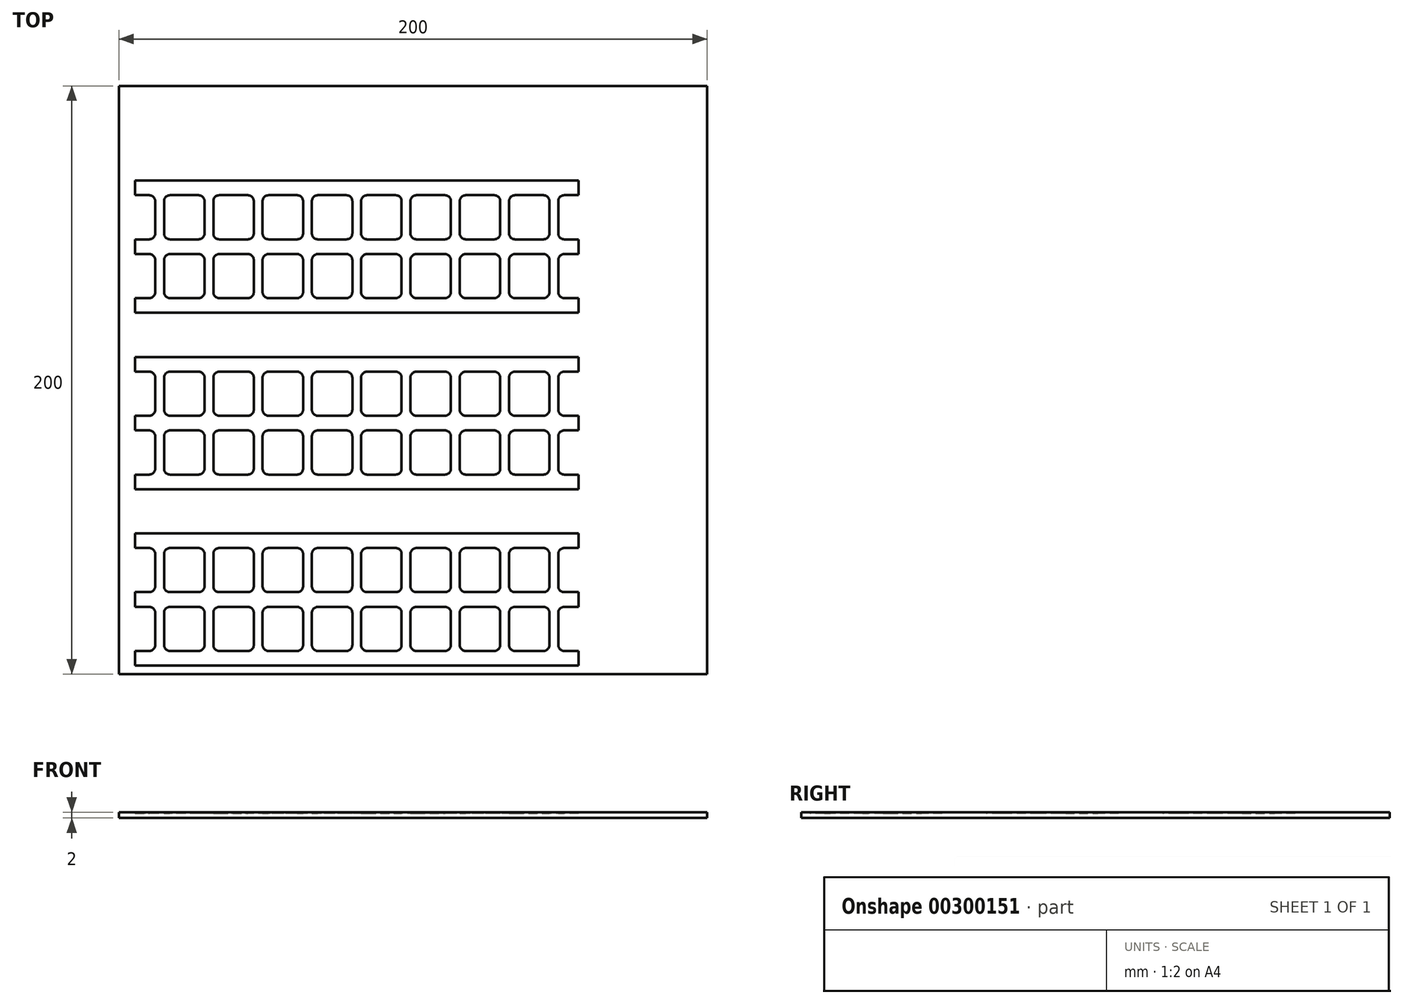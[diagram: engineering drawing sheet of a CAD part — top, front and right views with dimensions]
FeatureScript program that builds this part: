
annotation { "Feature Type Name" : "Feature", "Feature Type Description" : "" }
export const myFeature = defineFeature(function(context is Context, id is Id, definition is map)
    precondition{}
    {
        {
            var Q0;
            Q0=qCreatedBy(makeId("Top.planeOp"),FACE);
            var sketch = newSketch(context, id + "F0", { "sketchPlane" : qUnion([Q0])});
            skLineSegment(sketch, "E0.bottom", {"start": v(-3.5, 2.5) * mm, "end": v(-13.25, 2.5) * mm});
            skLineSegment(sketch, "E0.top", {"start": v(-3.5, 17.5) * mm, "end": v(-13.25, 17.5) * mm});
            skLineSegment(sketch, "E0.left", {"start": v(-1.5, 4.5) * mm, "end": v(-1.5, 15.5) * mm});
            skLineSegment(sketch, "E0.right", {"start": v(-15.25, 4.5) * mm, "end": v(-15.25, 15.5) * mm});
            skPoint(sketch, "E1.visualSharp", {"position": v(-15.25, 17.5) * mm});
            skArc(sketch, "E1.filletArc", {"start": v(-13.25, 17.5) * mm, "mid": v(-14.66, 16.91) * mm, "end": v(-15.25, 15.5) * mm});
            skPoint(sketch, "E2.visualSharp", {"position": v(-1.5, 17.5) * mm});
            skArc(sketch, "E2.filletArc", {"start": v(-1.5, 15.5) * mm, "mid": v(-2.09, 16.91) * mm, "end": v(-3.5, 17.5) * mm});
            skPoint(sketch, "E3.visualSharp", {"position": v(-1.5, 2.5) * mm});
            skArc(sketch, "E3.filletArc", {"start": v(-3.5, 2.5) * mm, "mid": v(-2.09, 3.09) * mm, "end": v(-1.5, 4.5) * mm});
            skPoint(sketch, "E4.visualSharp", {"position": v(-15.25, 2.5) * mm});
            skArc(sketch, "E4.filletArc", {"start": v(-15.25, 4.5) * mm, "mid": v(-14.66, 3.09) * mm, "end": v(-13.25, 2.5) * mm});
            skArc(sketch, "E5.MirrorCS", {"start": v(15.25, 4.5) * mm, "mid": v(14.66, 3.09) * mm, "end": v(13.25, 2.5) * mm});
            skArc(sketch, "E6.MirrorCS", {"start": v(13.25, 17.5) * mm, "mid": v(14.66, 16.91) * mm, "end": v(15.25, 15.5) * mm});
            skArc(sketch, "E7.MirrorCS", {"start": v(3.5, 2.5) * mm, "mid": v(2.09, 3.09) * mm, "end": v(1.5, 4.5) * mm});
            skArc(sketch, "E8.MirrorCS", {"start": v(1.5, 15.5) * mm, "mid": v(2.09, 16.91) * mm, "end": v(3.5, 17.5) * mm});
            skLineSegment(sketch, "E9.MirrorCS", {"start": v(3.5, 17.5) * mm, "end": v(13.25, 17.5) * mm});
            skLineSegment(sketch, "E10.MirrorCS", {"start": v(1.5, 4.5) * mm, "end": v(1.5, 15.5) * mm});
            skPoint(sketch, "E11.MirrorP", {"position": v(1.5, 17.5) * mm});
            skPoint(sketch, "E12.MirrorP", {"position": v(15.25, 2.5) * mm});
            skPoint(sketch, "E13.MirrorP", {"position": v(15.25, 17.5) * mm});
            skPoint(sketch, "E14.MirrorP", {"position": v(1.5, 2.5) * mm});
            skLineSegment(sketch, "E15.MirrorCS", {"start": v(3.5, 2.5) * mm, "end": v(13.25, 2.5) * mm});
            skLineSegment(sketch, "E16.MirrorCS", {"start": v(15.25, 4.5) * mm, "end": v(15.25, 15.5) * mm});
            skArc(sketch, "E17.MirrorCS", {"start": v(-1.5, -15.5) * mm, "mid": v(-2.09, -16.91) * mm, "end": v(-3.5, -17.5) * mm});
            skArc(sketch, "E18.MirrorCS", {"start": v(-3.5, -2.5) * mm, "mid": v(-2.09, -3.09) * mm, "end": v(-1.5, -4.5) * mm});
            skArc(sketch, "E19.MirrorCS", {"start": v(-13.25, -17.5) * mm, "mid": v(-14.66, -16.91) * mm, "end": v(-15.25, -15.5) * mm});
            skArc(sketch, "E20.MirrorCS", {"start": v(15.25, -4.5) * mm, "mid": v(14.66, -3.09) * mm, "end": v(13.25, -2.5) * mm});
            skArc(sketch, "E21.MirrorCS", {"start": v(-15.25, -4.5) * mm, "mid": v(-14.66, -3.09) * mm, "end": v(-13.25, -2.5) * mm});
            skArc(sketch, "E22.MirrorCS", {"start": v(13.25, -17.5) * mm, "mid": v(14.66, -16.91) * mm, "end": v(15.25, -15.5) * mm});
            skArc(sketch, "E23.MirrorCS", {"start": v(3.5, -2.5) * mm, "mid": v(2.09, -3.09) * mm, "end": v(1.5, -4.5) * mm});
            skArc(sketch, "E24.MirrorCS", {"start": v(1.5, -15.5) * mm, "mid": v(2.09, -16.91) * mm, "end": v(3.5, -17.5) * mm});
            skPoint(sketch, "E25.MirrorP", {"position": v(-15.25, -2.5) * mm});
            skLineSegment(sketch, "E26.MirrorCS", {"start": v(-1.5, -4.5) * mm, "end": v(-1.5, -15.5) * mm});
            skLineSegment(sketch, "E27.MirrorCS", {"start": v(15.25, -4.5) * mm, "end": v(15.25, -15.5) * mm});
            skPoint(sketch, "E28.MirrorP", {"position": v(-15.25, -17.5) * mm});
            skLineSegment(sketch, "E29.MirrorCS", {"start": v(3.5, -17.5) * mm, "end": v(13.25, -17.5) * mm});
            skLineSegment(sketch, "E30.MirrorCS", {"start": v(-15.25, -4.5) * mm, "end": v(-15.25, -15.5) * mm});
            skLineSegment(sketch, "E31.MirrorCS", {"start": v(-3.5, -17.5) * mm, "end": v(-13.25, -17.5) * mm});
            skPoint(sketch, "E32.MirrorP", {"position": v(-1.5, -17.5) * mm});
            skLineSegment(sketch, "E33.MirrorCS", {"start": v(1.5, -4.5) * mm, "end": v(1.5, -15.5) * mm});
            skLineSegment(sketch, "E34.MirrorCS", {"start": v(-3.5, -2.5) * mm, "end": v(-13.25, -2.5) * mm});
            skPoint(sketch, "E35.MirrorP", {"position": v(1.5, -17.5) * mm});
            skPoint(sketch, "E36.MirrorP", {"position": v(-1.5, -2.5) * mm});
            skPoint(sketch, "E37.MirrorP", {"position": v(15.25, -2.5) * mm});
            skPoint(sketch, "E38.MirrorP", {"position": v(15.25, -17.5) * mm});
            skPoint(sketch, "E39.MirrorP", {"position": v(1.5, -2.5) * mm});
            skLineSegment(sketch, "E40.MirrorCS", {"start": v(3.5, -2.5) * mm, "end": v(13.25, -2.5) * mm});
            skLineSegment(sketch, "E41", {"start": v(16.75, 36.36) * mm, "end": v(16.75, -33.16) * mm, "construction": true});
            skArc(sketch, "E42.MirrorCS", {"start": v(18.25, 4.5) * mm, "mid": v(18.84, 3.09) * mm, "end": v(20.25, 2.5) * mm});
            skArc(sketch, "E43.MirrorCS", {"start": v(20.25, -17.5) * mm, "mid": v(18.84, -16.91) * mm, "end": v(18.25, -15.5) * mm});
            skArc(sketch, "E44.MirrorCS", {"start": v(20.25, 17.5) * mm, "mid": v(18.84, 16.91) * mm, "end": v(18.25, 15.5) * mm});
            skArc(sketch, "E45.MirrorCS", {"start": v(18.25, -4.5) * mm, "mid": v(18.84, -3.09) * mm, "end": v(20.25, -2.5) * mm});
            skLineSegment(sketch, "E46.MirrorCS", {"start": v(25.12, -2.5) * mm, "end": v(20.25, -2.5) * mm});
            skLineSegment(sketch, "E47.MirrorCS", {"start": v(18.25, -4.5) * mm, "end": v(18.25, -15.5) * mm});
            skPoint(sketch, "E48.MirrorP", {"position": v(18.25, 2.5) * mm});
            skPoint(sketch, "E49.MirrorP", {"position": v(18.25, -2.5) * mm});
            skPoint(sketch, "E50.MirrorP", {"position": v(32, 2.5) * mm});
            skPoint(sketch, "E51.MirrorP", {"position": v(32, -2.5) * mm});
            skLineSegment(sketch, "E52.MirrorCS", {"start": v(25.12, 17.5) * mm, "end": v(20.25, 17.5) * mm});
            skPoint(sketch, "E53.MirrorP", {"position": v(18.25, -17.5) * mm});
            skPoint(sketch, "E54.MirrorP", {"position": v(32, 17.5) * mm});
            skLineSegment(sketch, "E55.MirrorCS", {"start": v(25.12, -17.5) * mm, "end": v(20.25, -17.5) * mm});
            skLineSegment(sketch, "E56.MirrorCS", {"start": v(18.25, 4.5) * mm, "end": v(18.25, 15.5) * mm});
            skPoint(sketch, "E57.MirrorP", {"position": v(18.25, 17.5) * mm});
            skLineSegment(sketch, "E58.MirrorCS", {"start": v(25.12, 2.5) * mm, "end": v(20.25, 2.5) * mm});
            skPoint(sketch, "E59.MirrorP", {"position": v(32, -17.5) * mm});
            skLineSegment(sketch, "E60.bottom", {"start": v(25.12, 22.5) * mm, "end": v(-25.12, 22.5) * mm});
            skLineSegment(sketch, "E60.top", {"start": v(25.12, -22.5) * mm, "end": v(-25.12, -22.5) * mm});
            skLineSegment(sketch, "E60.left", {"start": v(25.12, 22.5) * mm, "end": v(25.12, 17.5) * mm});
            skLineSegment(sketch, "E60.right", {"start": v(-25.12, 22.5) * mm, "end": v(-25.12, 17.5) * mm});
            skPoint(sketch, "E60.middle", {"position": v(0, 0) * mm});
            skArc(sketch, "E61.MirrorCS", {"start": v(-18.25, 4.5) * mm, "mid": v(-18.84, 3.09) * mm, "end": v(-20.25, 2.5) * mm});
            skArc(sketch, "E62.MirrorCS", {"start": v(-18.25, -4.5) * mm, "mid": v(-18.84, -3.09) * mm, "end": v(-20.25, -2.5) * mm});
            skArc(sketch, "E63.MirrorCS", {"start": v(-20.25, 17.5) * mm, "mid": v(-18.84, 16.91) * mm, "end": v(-18.25, 15.5) * mm});
            skArc(sketch, "E64.MirrorCS", {"start": v(-20.25, -17.5) * mm, "mid": v(-18.84, -16.91) * mm, "end": v(-18.25, -15.5) * mm});
            skPoint(sketch, "E65.MirrorP", {"position": v(-18.25, -2.5) * mm});
            skLineSegment(sketch, "E66.MirrorCS", {"start": v(-18.25, -4.5) * mm, "end": v(-18.25, -15.5) * mm});
            skPoint(sketch, "E67.MirrorP", {"position": v(-32, -17.5) * mm});
            skLineSegment(sketch, "E68.MirrorCS", {"start": v(-25.12, -2.5) * mm, "end": v(-20.25, -2.5) * mm});
            skPoint(sketch, "E69.MirrorP", {"position": v(-18.25, 2.5) * mm});
            skPoint(sketch, "E70.MirrorP", {"position": v(-18.25, 17.5) * mm});
            skPoint(sketch, "E71.MirrorP", {"position": v(-32, 17.5) * mm});
            skPoint(sketch, "E72.MirrorP", {"position": v(-18.25, -17.5) * mm});
            skLineSegment(sketch, "E73.MirrorCS", {"start": v(-25.12, 2.5) * mm, "end": v(-20.25, 2.5) * mm});
            skPoint(sketch, "E74.MirrorP", {"position": v(-32, 2.5) * mm});
            skPoint(sketch, "E75.MirrorP", {"position": v(-32, -2.5) * mm});
            skLineSegment(sketch, "E76.MirrorCS", {"start": v(-25.12, -17.5) * mm, "end": v(-20.25, -17.5) * mm});
            skLineSegment(sketch, "E77.MirrorCS", {"start": v(-25.12, 17.5) * mm, "end": v(-20.25, 17.5) * mm});
            skLineSegment(sketch, "E78.MirrorCS", {"start": v(-18.25, 4.5) * mm, "end": v(-18.25, 15.5) * mm});
            skLineSegment(sketch, "E79.trimOffspring", {"start": v(25.12, 2.5) * mm, "end": v(25.12, -2.5) * mm});
            skLineSegment(sketch, "E80.trimOffspring", {"start": v(25.12, -17.5) * mm, "end": v(25.12, -22.5) * mm});
            skPoint(sketch, "E81.MirrorCS.end.orphan", {"position": v(32, -4.5) * mm});
            skPoint(sketch, "E81.MirrorCS.start.orphan", {"position": v(30, -2.5) * mm});
            skPoint(sketch, "E82.MirrorCS.start.orphan", {"position": v(32, -15.5) * mm});
            skPoint(sketch, "E83.orphan", {"position": v(30, -17.5) * mm});
            skPoint(sketch, "E84.MirrorCS.start.orphan", {"position": v(30, 2.5) * mm});
            skPoint(sketch, "E85.MirrorCS.start.orphan", {"position": v(32, 4.5) * mm});
            skPoint(sketch, "E86.MirrorCS.end.orphan", {"position": v(30, 17.5) * mm});
            skPoint(sketch, "E86.MirrorCS.start.orphan", {"position": v(32, 15.5) * mm});
            skPoint(sketch, "E87.MirrorCS.start.orphan", {"position": v(-32, 15.5) * mm});
            skPoint(sketch, "E88.orphan", {"position": v(-30, 17.5) * mm});
            skLineSegment(sketch, "E89.trimOffspring", {"start": v(-25.12, 2.5) * mm, "end": v(-25.12, -2.5) * mm});
            skPoint(sketch, "E90.MirrorCS.end.orphan", {"position": v(-32, 4.5) * mm});
            skPoint(sketch, "E90.MirrorCS.start.orphan", {"position": v(-30, 2.5) * mm});
            skPoint(sketch, "E91.orphan", {"position": v(-30, -2.5) * mm});
            skPoint(sketch, "E92.MirrorCS.start.orphan", {"position": v(-32, -4.5) * mm});
            skPoint(sketch, "E93.MirrorCS.start.orphan", {"position": v(-32, -15.5) * mm});
            skPoint(sketch, "E94.orphan", {"position": v(-30, -17.5) * mm});
            skLineSegment(sketch, "E95.trimOffspring", {"start": v(-25.12, -17.5) * mm, "end": v(-25.12, -22.5) * mm});
            skLineSegment(sketch, "E96.0.1.0", {"start": v(1.5, 55.5) * mm, "end": v(1.5, 44.5) * mm});
            skPoint(sketch, "E96.0.1.1", {"position": v(30, 62.5) * mm});
            skLineSegment(sketch, "E96.0.1.2", {"start": v(-15.25, 64.5) * mm, "end": v(-15.25, 75.5) * mm});
            skPoint(sketch, "E96.0.1.3", {"position": v(1.5, 62.5) * mm});
            skLineSegment(sketch, "E96.0.1.4", {"start": v(-25.12, 62.5) * mm, "end": v(-20.25, 62.5) * mm});
            skPoint(sketch, "E96.0.1.5", {"position": v(15.25, 62.5) * mm});
            skPoint(sketch, "E96.0.1.6", {"position": v(-18.25, 77.5) * mm});
            skPoint(sketch, "E96.0.1.7", {"position": v(15.25, 42.5) * mm});
            skPoint(sketch, "E96.0.1.8", {"position": v(-18.25, 42.5) * mm});
            skLineSegment(sketch, "E96.0.1.9", {"start": v(25.12, 37.5) * mm, "end": v(-25.12, 37.5) * mm});
            skLineSegment(sketch, "E96.0.1.10", {"start": v(15.25, 64.5) * mm, "end": v(15.25, 75.5) * mm});
            skLineSegment(sketch, "E96.0.1.11", {"start": v(3.5, 62.5) * mm, "end": v(13.25, 62.5) * mm});
            skPoint(sketch, "E96.0.1.12", {"position": v(-1.5, 77.5) * mm});
            skPoint(sketch, "E96.0.1.13", {"position": v(1.5, 42.5) * mm});
            skPoint(sketch, "E96.0.1.14", {"position": v(-30, 62.5) * mm});
            skPoint(sketch, "E96.0.1.15", {"position": v(30, 42.5) * mm});
            skLineSegment(sketch, "E96.0.1.16", {"start": v(-25.12, 62.5) * mm, "end": v(-25.12, 57.5) * mm});
            skLineSegment(sketch, "E96.0.1.17", {"start": v(25.12, 57.5) * mm, "end": v(20.25, 57.5) * mm});
            skLineSegment(sketch, "E96.0.1.18", {"start": v(-3.5, 42.5) * mm, "end": v(-13.25, 42.5) * mm});
            skPoint(sketch, "E96.0.1.19", {"position": v(-15.25, 62.5) * mm});
            skLineSegment(sketch, "E96.0.1.20", {"start": v(3.5, 77.5) * mm, "end": v(13.25, 77.5) * mm});
            skPoint(sketch, "E96.0.1.21", {"position": v(-15.25, 77.5) * mm});
            skLineSegment(sketch, "E96.0.1.22", {"start": v(1.5, 64.5) * mm, "end": v(1.5, 75.5) * mm});
            skLineSegment(sketch, "E96.0.1.23", {"start": v(25.12, 77.5) * mm, "end": v(20.25, 77.5) * mm});
            skLineSegment(sketch, "E96.0.1.24", {"start": v(-25.12, 42.5) * mm, "end": v(-20.25, 42.5) * mm});
            skPoint(sketch, "E96.0.1.25", {"position": v(1.5, 57.5) * mm});
            skPoint(sketch, "E96.0.1.26", {"position": v(15.25, 57.5) * mm});
            skPoint(sketch, "E96.0.1.27", {"position": v(1.5, 77.5) * mm});
            skPoint(sketch, "E96.0.1.28", {"position": v(-1.5, 57.5) * mm});
            skPoint(sketch, "E96.0.1.29", {"position": v(0, 60) * mm});
            skLineSegment(sketch, "E96.0.1.30", {"start": v(-1.5, 64.5) * mm, "end": v(-1.5, 75.5) * mm});
            skLineSegment(sketch, "E96.0.1.31", {"start": v(-3.5, 57.5) * mm, "end": v(-13.25, 57.5) * mm});
            skLineSegment(sketch, "E96.0.1.32", {"start": v(-3.5, 77.5) * mm, "end": v(-13.25, 77.5) * mm});
            skLineSegment(sketch, "E96.0.1.33", {"start": v(-3.5, 62.5) * mm, "end": v(-13.25, 62.5) * mm});
            skPoint(sketch, "E96.0.1.34", {"position": v(30, 77.5) * mm});
            skLineSegment(sketch, "E96.0.1.35", {"start": v(25.12, 42.5) * mm, "end": v(20.25, 42.5) * mm});
            skPoint(sketch, "E96.0.1.36", {"position": v(18.25, 42.5) * mm});
            skPoint(sketch, "E96.0.1.37", {"position": v(-1.5, 42.5) * mm});
            skPoint(sketch, "E96.0.1.38", {"position": v(-30, 57.5) * mm});
            skPoint(sketch, "E96.0.1.39", {"position": v(-1.5, 62.5) * mm});
            skLineSegment(sketch, "E96.0.1.40", {"start": v(-18.25, 55.5) * mm, "end": v(-18.25, 44.5) * mm});
            skPoint(sketch, "E96.0.1.41", {"position": v(18.25, 62.5) * mm});
            skPoint(sketch, "E96.0.1.42", {"position": v(18.25, 57.5) * mm});
            skLineSegment(sketch, "E96.0.1.43", {"start": v(25.12, 62.5) * mm, "end": v(25.12, 57.5) * mm});
            skLineSegment(sketch, "E96.0.1.44", {"start": v(3.5, 42.5) * mm, "end": v(13.25, 42.5) * mm});
            skLineSegment(sketch, "E96.0.1.45", {"start": v(-1.5, 55.5) * mm, "end": v(-1.5, 44.5) * mm});
            skLineSegment(sketch, "E96.0.1.46", {"start": v(-15.25, 55.5) * mm, "end": v(-15.25, 44.5) * mm});
            skLineSegment(sketch, "E96.0.1.47", {"start": v(25.12, 82.5) * mm, "end": v(-25.12, 82.5) * mm});
            skPoint(sketch, "E96.0.1.48", {"position": v(-18.25, 62.5) * mm});
            skLineSegment(sketch, "E96.0.1.49", {"start": v(25.12, 62.5) * mm, "end": v(20.25, 62.5) * mm});
            skPoint(sketch, "E96.0.1.50", {"position": v(-18.25, 57.5) * mm});
            skLineSegment(sketch, "E96.0.1.51", {"start": v(-25.12, 57.5) * mm, "end": v(-20.25, 57.5) * mm});
            skPoint(sketch, "E96.0.1.52", {"position": v(-15.25, 57.5) * mm});
            skPoint(sketch, "E96.0.1.53", {"position": v(15.25, 77.5) * mm});
            skLineSegment(sketch, "E96.0.1.54", {"start": v(18.25, 55.5) * mm, "end": v(18.25, 44.5) * mm});
            skLineSegment(sketch, "E96.0.1.55", {"start": v(3.5, 57.5) * mm, "end": v(13.25, 57.5) * mm});
            skPoint(sketch, "E96.0.1.56", {"position": v(-30, 42.5) * mm});
            skPoint(sketch, "E96.0.1.57", {"position": v(-30, 77.5) * mm});
            skLineSegment(sketch, "E96.0.1.58", {"start": v(-25.12, 77.5) * mm, "end": v(-20.25, 77.5) * mm});
            skLineSegment(sketch, "E96.0.1.59", {"start": v(15.25, 55.5) * mm, "end": v(15.25, 44.5) * mm});
            skLineSegment(sketch, "E96.0.1.60", {"start": v(-18.25, 64.5) * mm, "end": v(-18.25, 75.5) * mm});
            skLineSegment(sketch, "E96.0.1.61", {"start": v(18.25, 64.5) * mm, "end": v(18.25, 75.5) * mm});
            skPoint(sketch, "E96.0.1.62", {"position": v(-15.25, 42.5) * mm});
            skPoint(sketch, "E96.0.1.63", {"position": v(30, 57.5) * mm});
            skPoint(sketch, "E96.0.1.64", {"position": v(18.25, 77.5) * mm});
            skLineSegment(sketch, "E96.0.1.65", {"start": v(-25.12, 62.5) * mm, "end": v(-25.12, 57.5) * mm});
            skArc(sketch, "E96.0.1.66", {"start": v(-13.25, 77.5) * mm, "mid": v(-14.66, 76.91) * mm, "end": v(-15.25, 75.5) * mm});
            skArc(sketch, "E96.0.1.67", {"start": v(-18.25, 64.5) * mm, "mid": v(-18.84, 63.09) * mm, "end": v(-20.25, 62.5) * mm});
            skArc(sketch, "E96.0.1.68", {"start": v(-15.25, 64.5) * mm, "mid": v(-14.66, 63.09) * mm, "end": v(-13.25, 62.5) * mm});
            skArc(sketch, "E96.0.1.69", {"start": v(13.25, 77.5) * mm, "mid": v(14.66, 76.91) * mm, "end": v(15.25, 75.5) * mm});
            skArc(sketch, "E96.0.1.70", {"start": v(15.25, 64.5) * mm, "mid": v(14.66, 63.09) * mm, "end": v(13.25, 62.5) * mm});
            skArc(sketch, "E96.0.1.71", {"start": v(-1.5, 44.5) * mm, "mid": v(-2.09, 43.09) * mm, "end": v(-3.5, 42.5) * mm});
            skArc(sketch, "E96.0.1.72", {"start": v(3.5, 62.5) * mm, "mid": v(2.09, 63.09) * mm, "end": v(1.5, 64.5) * mm});
            skArc(sketch, "E96.0.1.73", {"start": v(1.5, 44.5) * mm, "mid": v(2.09, 43.09) * mm, "end": v(3.5, 42.5) * mm});
            skArc(sketch, "E96.0.1.74", {"start": v(-3.5, 62.5) * mm, "mid": v(-2.09, 63.09) * mm, "end": v(-1.5, 64.5) * mm});
            skArc(sketch, "E96.0.1.75", {"start": v(-18.25, 55.5) * mm, "mid": v(-18.84, 56.91) * mm, "end": v(-20.25, 57.5) * mm});
            skArc(sketch, "E96.0.1.76", {"start": v(-1.5, 75.5) * mm, "mid": v(-2.09, 76.91) * mm, "end": v(-3.5, 77.5) * mm});
            skArc(sketch, "E96.0.1.77", {"start": v(-3.5, 57.5) * mm, "mid": v(-2.09, 56.91) * mm, "end": v(-1.5, 55.5) * mm});
            skLineSegment(sketch, "E96.0.1.78", {"start": v(25.12, 82.5) * mm, "end": v(25.12, 77.5) * mm});
            skArc(sketch, "E96.0.1.79", {"start": v(13.25, 42.5) * mm, "mid": v(14.66, 43.09) * mm, "end": v(15.25, 44.5) * mm});
            skArc(sketch, "E96.0.1.80", {"start": v(3.5, 57.5) * mm, "mid": v(2.09, 56.91) * mm, "end": v(1.5, 55.5) * mm});
            skArc(sketch, "E96.0.1.81", {"start": v(1.5, 75.5) * mm, "mid": v(2.09, 76.91) * mm, "end": v(3.5, 77.5) * mm});
            skArc(sketch, "E96.0.1.82", {"start": v(18.25, 64.5) * mm, "mid": v(18.84, 63.09) * mm, "end": v(20.25, 62.5) * mm});
            skArc(sketch, "E96.0.1.83", {"start": v(18.25, 55.5) * mm, "mid": v(18.84, 56.91) * mm, "end": v(20.25, 57.5) * mm});
            skArc(sketch, "E96.0.1.84", {"start": v(20.25, 77.5) * mm, "mid": v(18.84, 76.91) * mm, "end": v(18.25, 75.5) * mm});
            skLineSegment(sketch, "E96.0.1.85", {"start": v(25.12, 42.5) * mm, "end": v(25.12, 37.5) * mm});
            skArc(sketch, "E96.0.1.86", {"start": v(-15.25, 55.5) * mm, "mid": v(-14.66, 56.91) * mm, "end": v(-13.25, 57.5) * mm});
            skArc(sketch, "E96.0.1.87", {"start": v(15.25, 55.5) * mm, "mid": v(14.66, 56.91) * mm, "end": v(13.25, 57.5) * mm});
            skArc(sketch, "E96.0.1.88", {"start": v(-13.25, 42.5) * mm, "mid": v(-14.66, 43.09) * mm, "end": v(-15.25, 44.5) * mm});
            skArc(sketch, "E96.0.1.89", {"start": v(-20.25, 42.5) * mm, "mid": v(-18.84, 43.09) * mm, "end": v(-18.25, 44.5) * mm});
            skArc(sketch, "E96.0.1.90", {"start": v(20.25, 42.5) * mm, "mid": v(18.84, 43.09) * mm, "end": v(18.25, 44.5) * mm});
            skArc(sketch, "E96.0.1.91", {"start": v(-20.25, 77.5) * mm, "mid": v(-18.84, 76.91) * mm, "end": v(-18.25, 75.5) * mm});
            skLineSegment(sketch, "E96.0.1.92", {"start": v(-25.12, 42.5) * mm, "end": v(-25.12, 37.5) * mm});
            skLineSegment(sketch, "E96.0.1.93", {"start": v(-25.12, 82.5) * mm, "end": v(-25.12, 77.5) * mm});
            skLineSegment(sketch, "E96.0.1.94", {"start": v(-25.12, 82.5) * mm, "end": v(-25.12, 77.5) * mm});
            skLineSegment(sketch, "E96.0.1.95", {"start": v(-25.12, 42.5) * mm, "end": v(-25.12, 37.5) * mm});
            skLineSegment(sketch, "E96.0.2.0", {"start": v(1.5, 115.5) * mm, "end": v(1.5, 104.5) * mm});
            skPoint(sketch, "E96.0.2.1", {"position": v(30, 122.5) * mm});
            skLineSegment(sketch, "E96.0.2.2", {"start": v(-15.25, 124.5) * mm, "end": v(-15.25, 135.5) * mm});
            skPoint(sketch, "E96.0.2.3", {"position": v(1.5, 122.5) * mm});
            skLineSegment(sketch, "E96.0.2.4", {"start": v(-25.12, 122.5) * mm, "end": v(-20.25, 122.5) * mm});
            skPoint(sketch, "E96.0.2.5", {"position": v(15.25, 122.5) * mm});
            skPoint(sketch, "E96.0.2.6", {"position": v(-18.25, 137.5) * mm});
            skPoint(sketch, "E96.0.2.7", {"position": v(15.25, 102.5) * mm});
            skPoint(sketch, "E96.0.2.8", {"position": v(-18.25, 102.5) * mm});
            skLineSegment(sketch, "E96.0.2.9", {"start": v(25.12, 97.5) * mm, "end": v(-25.12, 97.5) * mm});
            skLineSegment(sketch, "E96.0.2.10", {"start": v(15.25, 124.5) * mm, "end": v(15.25, 135.5) * mm});
            skLineSegment(sketch, "E96.0.2.11", {"start": v(3.5, 122.5) * mm, "end": v(13.25, 122.5) * mm});
            skPoint(sketch, "E96.0.2.12", {"position": v(-1.5, 137.5) * mm});
            skPoint(sketch, "E96.0.2.13", {"position": v(1.5, 102.5) * mm});
            skPoint(sketch, "E96.0.2.14", {"position": v(-30, 122.5) * mm});
            skPoint(sketch, "E96.0.2.15", {"position": v(30, 102.5) * mm});
            skLineSegment(sketch, "E96.0.2.16", {"start": v(-25.12, 122.5) * mm, "end": v(-25.12, 117.5) * mm});
            skLineSegment(sketch, "E96.0.2.17", {"start": v(25.12, 117.5) * mm, "end": v(20.25, 117.5) * mm});
            skLineSegment(sketch, "E96.0.2.18", {"start": v(-3.5, 102.5) * mm, "end": v(-13.25, 102.5) * mm});
            skPoint(sketch, "E96.0.2.19", {"position": v(-15.25, 122.5) * mm});
            skLineSegment(sketch, "E96.0.2.20", {"start": v(3.5, 137.5) * mm, "end": v(13.25, 137.5) * mm});
            skPoint(sketch, "E96.0.2.21", {"position": v(-15.25, 137.5) * mm});
            skLineSegment(sketch, "E96.0.2.22", {"start": v(1.5, 124.5) * mm, "end": v(1.5, 135.5) * mm});
            skLineSegment(sketch, "E96.0.2.23", {"start": v(25.12, 137.5) * mm, "end": v(20.25, 137.5) * mm});
            skLineSegment(sketch, "E96.0.2.24", {"start": v(-25.12, 102.5) * mm, "end": v(-20.25, 102.5) * mm});
            skPoint(sketch, "E96.0.2.25", {"position": v(1.5, 117.5) * mm});
            skPoint(sketch, "E96.0.2.26", {"position": v(15.25, 117.5) * mm});
            skPoint(sketch, "E96.0.2.27", {"position": v(1.5, 137.5) * mm});
            skPoint(sketch, "E96.0.2.28", {"position": v(-1.5, 117.5) * mm});
            skPoint(sketch, "E96.0.2.29", {"position": v(0, 120) * mm});
            skLineSegment(sketch, "E96.0.2.30", {"start": v(-1.5, 124.5) * mm, "end": v(-1.5, 135.5) * mm});
            skLineSegment(sketch, "E96.0.2.31", {"start": v(-3.5, 117.5) * mm, "end": v(-13.25, 117.5) * mm});
            skLineSegment(sketch, "E96.0.2.32", {"start": v(-3.5, 137.5) * mm, "end": v(-13.25, 137.5) * mm});
            skLineSegment(sketch, "E96.0.2.33", {"start": v(-3.5, 122.5) * mm, "end": v(-13.25, 122.5) * mm});
            skPoint(sketch, "E96.0.2.34", {"position": v(30, 137.5) * mm});
            skLineSegment(sketch, "E96.0.2.35", {"start": v(25.12, 102.5) * mm, "end": v(20.25, 102.5) * mm});
            skPoint(sketch, "E96.0.2.36", {"position": v(18.25, 102.5) * mm});
            skPoint(sketch, "E96.0.2.37", {"position": v(-1.5, 102.5) * mm});
            skPoint(sketch, "E96.0.2.38", {"position": v(-30, 117.5) * mm});
            skPoint(sketch, "E96.0.2.39", {"position": v(-1.5, 122.5) * mm});
            skLineSegment(sketch, "E96.0.2.40", {"start": v(-18.25, 115.5) * mm, "end": v(-18.25, 104.5) * mm});
            skPoint(sketch, "E96.0.2.41", {"position": v(18.25, 122.5) * mm});
            skPoint(sketch, "E96.0.2.42", {"position": v(18.25, 117.5) * mm});
            skLineSegment(sketch, "E96.0.2.43", {"start": v(25.12, 122.5) * mm, "end": v(25.12, 117.5) * mm});
            skLineSegment(sketch, "E96.0.2.44", {"start": v(3.5, 102.5) * mm, "end": v(13.25, 102.5) * mm});
            skLineSegment(sketch, "E96.0.2.45", {"start": v(-1.5, 115.5) * mm, "end": v(-1.5, 104.5) * mm});
            skLineSegment(sketch, "E96.0.2.46", {"start": v(-15.25, 115.5) * mm, "end": v(-15.25, 104.5) * mm});
            skLineSegment(sketch, "E96.0.2.47", {"start": v(25.12, 142.5) * mm, "end": v(-25.12, 142.5) * mm});
            skPoint(sketch, "E96.0.2.48", {"position": v(-18.25, 122.5) * mm});
            skLineSegment(sketch, "E96.0.2.49", {"start": v(25.12, 122.5) * mm, "end": v(20.25, 122.5) * mm});
            skPoint(sketch, "E96.0.2.50", {"position": v(-18.25, 117.5) * mm});
            skLineSegment(sketch, "E96.0.2.51", {"start": v(-25.12, 117.5) * mm, "end": v(-20.25, 117.5) * mm});
            skPoint(sketch, "E96.0.2.52", {"position": v(-15.25, 117.5) * mm});
            skPoint(sketch, "E96.0.2.53", {"position": v(15.25, 137.5) * mm});
            skLineSegment(sketch, "E96.0.2.54", {"start": v(18.25, 115.5) * mm, "end": v(18.25, 104.5) * mm});
            skLineSegment(sketch, "E96.0.2.55", {"start": v(3.5, 117.5) * mm, "end": v(13.25, 117.5) * mm});
            skPoint(sketch, "E96.0.2.56", {"position": v(-30, 102.5) * mm});
            skPoint(sketch, "E96.0.2.57", {"position": v(-30, 137.5) * mm});
            skLineSegment(sketch, "E96.0.2.58", {"start": v(-25.12, 137.5) * mm, "end": v(-20.25, 137.5) * mm});
            skLineSegment(sketch, "E96.0.2.59", {"start": v(15.25, 115.5) * mm, "end": v(15.25, 104.5) * mm});
            skLineSegment(sketch, "E96.0.2.60", {"start": v(-18.25, 124.5) * mm, "end": v(-18.25, 135.5) * mm});
            skLineSegment(sketch, "E96.0.2.61", {"start": v(18.25, 124.5) * mm, "end": v(18.25, 135.5) * mm});
            skPoint(sketch, "E96.0.2.62", {"position": v(-15.25, 102.5) * mm});
            skPoint(sketch, "E96.0.2.63", {"position": v(30, 117.5) * mm});
            skPoint(sketch, "E96.0.2.64", {"position": v(18.25, 137.5) * mm});
            skLineSegment(sketch, "E96.0.2.65", {"start": v(-25.12, 122.5) * mm, "end": v(-25.12, 117.5) * mm});
            skArc(sketch, "E96.0.2.66", {"start": v(-13.25, 137.5) * mm, "mid": v(-14.66, 136.91) * mm, "end": v(-15.25, 135.5) * mm});
            skArc(sketch, "E96.0.2.67", {"start": v(-18.25, 124.5) * mm, "mid": v(-18.84, 123.09) * mm, "end": v(-20.25, 122.5) * mm});
            skArc(sketch, "E96.0.2.68", {"start": v(-15.25, 124.5) * mm, "mid": v(-14.66, 123.09) * mm, "end": v(-13.25, 122.5) * mm});
            skArc(sketch, "E96.0.2.69", {"start": v(13.25, 137.5) * mm, "mid": v(14.66, 136.91) * mm, "end": v(15.25, 135.5) * mm});
            skArc(sketch, "E96.0.2.70", {"start": v(15.25, 124.5) * mm, "mid": v(14.66, 123.09) * mm, "end": v(13.25, 122.5) * mm});
            skArc(sketch, "E96.0.2.71", {"start": v(-1.5, 104.5) * mm, "mid": v(-2.09, 103.09) * mm, "end": v(-3.5, 102.5) * mm});
            skArc(sketch, "E96.0.2.72", {"start": v(3.5, 122.5) * mm, "mid": v(2.09, 123.09) * mm, "end": v(1.5, 124.5) * mm});
            skArc(sketch, "E96.0.2.73", {"start": v(1.5, 104.5) * mm, "mid": v(2.09, 103.09) * mm, "end": v(3.5, 102.5) * mm});
            skArc(sketch, "E96.0.2.74", {"start": v(-3.5, 122.5) * mm, "mid": v(-2.09, 123.09) * mm, "end": v(-1.5, 124.5) * mm});
            skArc(sketch, "E96.0.2.75", {"start": v(-18.25, 115.5) * mm, "mid": v(-18.84, 116.91) * mm, "end": v(-20.25, 117.5) * mm});
            skArc(sketch, "E96.0.2.76", {"start": v(-1.5, 135.5) * mm, "mid": v(-2.09, 136.91) * mm, "end": v(-3.5, 137.5) * mm});
            skArc(sketch, "E96.0.2.77", {"start": v(-3.5, 117.5) * mm, "mid": v(-2.09, 116.91) * mm, "end": v(-1.5, 115.5) * mm});
            skLineSegment(sketch, "E96.0.2.78", {"start": v(25.12, 142.5) * mm, "end": v(25.12, 137.5) * mm});
            skArc(sketch, "E96.0.2.79", {"start": v(13.25, 102.5) * mm, "mid": v(14.66, 103.09) * mm, "end": v(15.25, 104.5) * mm});
            skArc(sketch, "E96.0.2.80", {"start": v(3.5, 117.5) * mm, "mid": v(2.09, 116.91) * mm, "end": v(1.5, 115.5) * mm});
            skArc(sketch, "E96.0.2.81", {"start": v(1.5, 135.5) * mm, "mid": v(2.09, 136.91) * mm, "end": v(3.5, 137.5) * mm});
            skArc(sketch, "E96.0.2.82", {"start": v(18.25, 124.5) * mm, "mid": v(18.84, 123.09) * mm, "end": v(20.25, 122.5) * mm});
            skArc(sketch, "E96.0.2.83", {"start": v(18.25, 115.5) * mm, "mid": v(18.84, 116.91) * mm, "end": v(20.25, 117.5) * mm});
            skArc(sketch, "E96.0.2.84", {"start": v(20.25, 137.5) * mm, "mid": v(18.84, 136.91) * mm, "end": v(18.25, 135.5) * mm});
            skLineSegment(sketch, "E96.0.2.85", {"start": v(25.12, 102.5) * mm, "end": v(25.12, 97.5) * mm});
            skArc(sketch, "E96.0.2.86", {"start": v(-15.25, 115.5) * mm, "mid": v(-14.66, 116.91) * mm, "end": v(-13.25, 117.5) * mm});
            skArc(sketch, "E96.0.2.87", {"start": v(15.25, 115.5) * mm, "mid": v(14.66, 116.91) * mm, "end": v(13.25, 117.5) * mm});
            skArc(sketch, "E96.0.2.88", {"start": v(-13.25, 102.5) * mm, "mid": v(-14.66, 103.09) * mm, "end": v(-15.25, 104.5) * mm});
            skArc(sketch, "E96.0.2.89", {"start": v(-20.25, 102.5) * mm, "mid": v(-18.84, 103.09) * mm, "end": v(-18.25, 104.5) * mm});
            skArc(sketch, "E96.0.2.90", {"start": v(20.25, 102.5) * mm, "mid": v(18.84, 103.09) * mm, "end": v(18.25, 104.5) * mm});
            skArc(sketch, "E96.0.2.91", {"start": v(-20.25, 137.5) * mm, "mid": v(-18.84, 136.91) * mm, "end": v(-18.25, 135.5) * mm});
            skLineSegment(sketch, "E96.0.2.92", {"start": v(-25.12, 102.5) * mm, "end": v(-25.12, 97.5) * mm});
            skLineSegment(sketch, "E96.0.2.93", {"start": v(-25.12, 142.5) * mm, "end": v(-25.12, 137.5) * mm});
            skLineSegment(sketch, "E96.0.2.94", {"start": v(-25.12, 142.5) * mm, "end": v(-25.12, 137.5) * mm});
            skLineSegment(sketch, "E96.0.2.95", {"start": v(-25.12, 102.5) * mm, "end": v(-25.12, 97.5) * mm});
            skLineSegment(sketch, "E96.1.0.0", {"start": v(51.75, -4.5) * mm, "end": v(51.75, -15.5) * mm});
            skPoint(sketch, "E96.1.0.1", {"position": v(80.25, 2.5) * mm});
            skLineSegment(sketch, "E96.1.0.2", {"start": v(35, 4.5) * mm, "end": v(35, 15.5) * mm});
            skPoint(sketch, "E96.1.0.3", {"position": v(51.75, 2.5) * mm});
            skLineSegment(sketch, "E96.1.0.4", {"start": v(25.12, 2.5) * mm, "end": v(30, 2.5) * mm});
            skPoint(sketch, "E96.1.0.5", {"position": v(65.5, 2.5) * mm});
            skPoint(sketch, "E96.1.0.7", {"position": v(65.5, -17.5) * mm});
            skLineSegment(sketch, "E96.1.0.9", {"start": v(75.38, -22.5) * mm, "end": v(25.12, -22.5) * mm});
            skLineSegment(sketch, "E96.1.0.10", {"start": v(65.5, 4.5) * mm, "end": v(65.5, 15.5) * mm});
            skLineSegment(sketch, "E96.1.0.11", {"start": v(53.75, 2.5) * mm, "end": v(63.5, 2.5) * mm});
            skPoint(sketch, "E96.1.0.12", {"position": v(48.75, 17.5) * mm});
            skPoint(sketch, "E96.1.0.13", {"position": v(51.75, -17.5) * mm});
            skPoint(sketch, "E96.1.0.14", {"position": v(20.25, 2.5) * mm});
            skPoint(sketch, "E96.1.0.15", {"position": v(80.25, -17.5) * mm});
            skLineSegment(sketch, "E96.1.0.17", {"start": v(75.38, -2.5) * mm, "end": v(70.5, -2.5) * mm});
            skLineSegment(sketch, "E96.1.0.18", {"start": v(46.75, -17.5) * mm, "end": v(37, -17.5) * mm});
            skPoint(sketch, "E96.1.0.19", {"position": v(35, 2.5) * mm});
            skLineSegment(sketch, "E96.1.0.20", {"start": v(53.75, 17.5) * mm, "end": v(63.5, 17.5) * mm});
            skPoint(sketch, "E96.1.0.21", {"position": v(35, 17.5) * mm});
            skLineSegment(sketch, "E96.1.0.22", {"start": v(51.75, 4.5) * mm, "end": v(51.75, 15.5) * mm});
            skLineSegment(sketch, "E96.1.0.23", {"start": v(75.38, 17.5) * mm, "end": v(70.5, 17.5) * mm});
            skLineSegment(sketch, "E96.1.0.24", {"start": v(25.12, -17.5) * mm, "end": v(30, -17.5) * mm});
            skPoint(sketch, "E96.1.0.25", {"position": v(51.75, -2.5) * mm});
            skPoint(sketch, "E96.1.0.26", {"position": v(65.5, -2.5) * mm});
            skPoint(sketch, "E96.1.0.27", {"position": v(51.75, 17.5) * mm});
            skPoint(sketch, "E96.1.0.28", {"position": v(48.75, -2.5) * mm});
            skPoint(sketch, "E96.1.0.29", {"position": v(50.25, 0) * mm});
            skLineSegment(sketch, "E96.1.0.30", {"start": v(48.75, 4.5) * mm, "end": v(48.75, 15.5) * mm});
            skLineSegment(sketch, "E96.1.0.31", {"start": v(46.75, -2.5) * mm, "end": v(37, -2.5) * mm});
            skLineSegment(sketch, "E96.1.0.32", {"start": v(46.75, 17.5) * mm, "end": v(37, 17.5) * mm});
            skLineSegment(sketch, "E96.1.0.33", {"start": v(46.75, 2.5) * mm, "end": v(37, 2.5) * mm});
            skPoint(sketch, "E96.1.0.34", {"position": v(80.25, 17.5) * mm});
            skLineSegment(sketch, "E96.1.0.35", {"start": v(75.38, -17.5) * mm, "end": v(70.5, -17.5) * mm});
            skPoint(sketch, "E96.1.0.36", {"position": v(68.5, -17.5) * mm});
            skPoint(sketch, "E96.1.0.37", {"position": v(48.75, -17.5) * mm});
            skPoint(sketch, "E96.1.0.38", {"position": v(20.25, -2.5) * mm});
            skPoint(sketch, "E96.1.0.39", {"position": v(48.75, 2.5) * mm});
            skLineSegment(sketch, "E96.1.0.40", {"start": v(32, -4.5) * mm, "end": v(32, -15.5) * mm});
            skPoint(sketch, "E96.1.0.41", {"position": v(68.5, 2.5) * mm});
            skPoint(sketch, "E96.1.0.42", {"position": v(68.5, -2.5) * mm});
            skLineSegment(sketch, "E96.1.0.43", {"start": v(75.38, 2.5) * mm, "end": v(75.38, -2.5) * mm});
            skLineSegment(sketch, "E96.1.0.44", {"start": v(53.75, -17.5) * mm, "end": v(63.5, -17.5) * mm});
            skLineSegment(sketch, "E96.1.0.45", {"start": v(48.75, -4.5) * mm, "end": v(48.75, -15.5) * mm});
            skLineSegment(sketch, "E96.1.0.46", {"start": v(35, -4.5) * mm, "end": v(35, -15.5) * mm});
            skLineSegment(sketch, "E96.1.0.47", {"start": v(75.38, 22.5) * mm, "end": v(25.12, 22.5) * mm});
            skLineSegment(sketch, "E96.1.0.49", {"start": v(75.38, 2.5) * mm, "end": v(70.5, 2.5) * mm});
            skLineSegment(sketch, "E96.1.0.51", {"start": v(25.12, -2.5) * mm, "end": v(30, -2.5) * mm});
            skPoint(sketch, "E96.1.0.52", {"position": v(35, -2.5) * mm});
            skPoint(sketch, "E96.1.0.53", {"position": v(65.5, 17.5) * mm});
            skLineSegment(sketch, "E96.1.0.54", {"start": v(68.5, -4.5) * mm, "end": v(68.5, -15.5) * mm});
            skLineSegment(sketch, "E96.1.0.55", {"start": v(53.75, -2.5) * mm, "end": v(63.5, -2.5) * mm});
            skPoint(sketch, "E96.1.0.56", {"position": v(20.25, -17.5) * mm});
            skPoint(sketch, "E96.1.0.57", {"position": v(20.25, 17.5) * mm});
            skLineSegment(sketch, "E96.1.0.58", {"start": v(25.12, 17.5) * mm, "end": v(30, 17.5) * mm});
            skLineSegment(sketch, "E96.1.0.59", {"start": v(65.5, -4.5) * mm, "end": v(65.5, -15.5) * mm});
            skLineSegment(sketch, "E96.1.0.60", {"start": v(32, 4.5) * mm, "end": v(32, 15.5) * mm});
            skLineSegment(sketch, "E96.1.0.61", {"start": v(68.5, 4.5) * mm, "end": v(68.5, 15.5) * mm});
            skPoint(sketch, "E96.1.0.62", {"position": v(35, -17.5) * mm});
            skPoint(sketch, "E96.1.0.63", {"position": v(80.25, -2.5) * mm});
            skPoint(sketch, "E96.1.0.64", {"position": v(68.5, 17.5) * mm});
            skArc(sketch, "E96.1.0.66", {"start": v(37, 17.5) * mm, "mid": v(35.59, 16.91) * mm, "end": v(35, 15.5) * mm});
            skArc(sketch, "E96.1.0.67", {"start": v(32, 4.5) * mm, "mid": v(31.41, 3.09) * mm, "end": v(30, 2.5) * mm});
            skArc(sketch, "E96.1.0.68", {"start": v(35, 4.5) * mm, "mid": v(35.59, 3.09) * mm, "end": v(37, 2.5) * mm});
            skArc(sketch, "E96.1.0.69", {"start": v(63.5, 17.5) * mm, "mid": v(64.91, 16.91) * mm, "end": v(65.5, 15.5) * mm});
            skArc(sketch, "E96.1.0.70", {"start": v(65.5, 4.5) * mm, "mid": v(64.91, 3.09) * mm, "end": v(63.5, 2.5) * mm});
            skArc(sketch, "E96.1.0.71", {"start": v(48.75, -15.5) * mm, "mid": v(48.16, -16.91) * mm, "end": v(46.75, -17.5) * mm});
            skArc(sketch, "E96.1.0.72", {"start": v(53.75, 2.5) * mm, "mid": v(52.34, 3.09) * mm, "end": v(51.75, 4.5) * mm});
            skArc(sketch, "E96.1.0.73", {"start": v(51.75, -15.5) * mm, "mid": v(52.34, -16.91) * mm, "end": v(53.75, -17.5) * mm});
            skArc(sketch, "E96.1.0.74", {"start": v(46.75, 2.5) * mm, "mid": v(48.16, 3.09) * mm, "end": v(48.75, 4.5) * mm});
            skArc(sketch, "E96.1.0.75", {"start": v(32, -4.5) * mm, "mid": v(31.41, -3.09) * mm, "end": v(30, -2.5) * mm});
            skArc(sketch, "E96.1.0.76", {"start": v(48.75, 15.5) * mm, "mid": v(48.16, 16.91) * mm, "end": v(46.75, 17.5) * mm});
            skArc(sketch, "E96.1.0.77", {"start": v(46.75, -2.5) * mm, "mid": v(48.16, -3.09) * mm, "end": v(48.75, -4.5) * mm});
            skLineSegment(sketch, "E96.1.0.78", {"start": v(75.38, 22.5) * mm, "end": v(75.38, 17.5) * mm});
            skArc(sketch, "E96.1.0.79", {"start": v(63.5, -17.5) * mm, "mid": v(64.91, -16.91) * mm, "end": v(65.5, -15.5) * mm});
            skArc(sketch, "E96.1.0.80", {"start": v(53.75, -2.5) * mm, "mid": v(52.34, -3.09) * mm, "end": v(51.75, -4.5) * mm});
            skArc(sketch, "E96.1.0.81", {"start": v(51.75, 15.5) * mm, "mid": v(52.34, 16.91) * mm, "end": v(53.75, 17.5) * mm});
            skArc(sketch, "E96.1.0.82", {"start": v(68.5, 4.5) * mm, "mid": v(69.09, 3.09) * mm, "end": v(70.5, 2.5) * mm});
            skArc(sketch, "E96.1.0.83", {"start": v(68.5, -4.5) * mm, "mid": v(69.09, -3.09) * mm, "end": v(70.5, -2.5) * mm});
            skArc(sketch, "E96.1.0.84", {"start": v(70.5, 17.5) * mm, "mid": v(69.09, 16.91) * mm, "end": v(68.5, 15.5) * mm});
            skLineSegment(sketch, "E96.1.0.85", {"start": v(75.38, -17.5) * mm, "end": v(75.38, -22.5) * mm});
            skArc(sketch, "E96.1.0.86", {"start": v(35, -4.5) * mm, "mid": v(35.59, -3.09) * mm, "end": v(37, -2.5) * mm});
            skArc(sketch, "E96.1.0.87", {"start": v(65.5, -4.5) * mm, "mid": v(64.91, -3.09) * mm, "end": v(63.5, -2.5) * mm});
            skArc(sketch, "E96.1.0.88", {"start": v(37, -17.5) * mm, "mid": v(35.59, -16.91) * mm, "end": v(35, -15.5) * mm});
            skArc(sketch, "E96.1.0.89", {"start": v(30, -17.5) * mm, "mid": v(31.41, -16.91) * mm, "end": v(32, -15.5) * mm});
            skArc(sketch, "E96.1.0.90", {"start": v(70.5, -17.5) * mm, "mid": v(69.09, -16.91) * mm, "end": v(68.5, -15.5) * mm});
            skArc(sketch, "E96.1.0.91", {"start": v(30, 17.5) * mm, "mid": v(31.41, 16.91) * mm, "end": v(32, 15.5) * mm});
            skLineSegment(sketch, "E96.1.1.0", {"start": v(51.75, 55.5) * mm, "end": v(51.75, 44.5) * mm});
            skPoint(sketch, "E96.1.1.1", {"position": v(80.25, 62.5) * mm});
            skLineSegment(sketch, "E96.1.1.2", {"start": v(35, 64.5) * mm, "end": v(35, 75.5) * mm});
            skPoint(sketch, "E96.1.1.3", {"position": v(51.75, 62.5) * mm});
            skLineSegment(sketch, "E96.1.1.4", {"start": v(25.12, 62.5) * mm, "end": v(30, 62.5) * mm});
            skPoint(sketch, "E96.1.1.5", {"position": v(65.5, 62.5) * mm});
            skPoint(sketch, "E96.1.1.6", {"position": v(32, 77.5) * mm});
            skPoint(sketch, "E96.1.1.7", {"position": v(65.5, 42.5) * mm});
            skPoint(sketch, "E96.1.1.8", {"position": v(32, 42.5) * mm});
            skLineSegment(sketch, "E96.1.1.9", {"start": v(75.38, 37.5) * mm, "end": v(25.12, 37.5) * mm});
            skLineSegment(sketch, "E96.1.1.10", {"start": v(65.5, 64.5) * mm, "end": v(65.5, 75.5) * mm});
            skLineSegment(sketch, "E96.1.1.11", {"start": v(53.75, 62.5) * mm, "end": v(63.5, 62.5) * mm});
            skPoint(sketch, "E96.1.1.12", {"position": v(48.75, 77.5) * mm});
            skPoint(sketch, "E96.1.1.13", {"position": v(51.75, 42.5) * mm});
            skPoint(sketch, "E96.1.1.14", {"position": v(20.25, 62.5) * mm});
            skPoint(sketch, "E96.1.1.15", {"position": v(80.25, 42.5) * mm});
            skLineSegment(sketch, "E96.1.1.16", {"start": v(25.12, 62.5) * mm, "end": v(25.12, 57.5) * mm});
            skLineSegment(sketch, "E96.1.1.17", {"start": v(75.38, 57.5) * mm, "end": v(70.5, 57.5) * mm});
            skLineSegment(sketch, "E96.1.1.18", {"start": v(46.75, 42.5) * mm, "end": v(37, 42.5) * mm});
            skPoint(sketch, "E96.1.1.19", {"position": v(35, 62.5) * mm});
            skLineSegment(sketch, "E96.1.1.20", {"start": v(53.75, 77.5) * mm, "end": v(63.5, 77.5) * mm});
            skPoint(sketch, "E96.1.1.21", {"position": v(35, 77.5) * mm});
            skLineSegment(sketch, "E96.1.1.22", {"start": v(51.75, 64.5) * mm, "end": v(51.75, 75.5) * mm});
            skLineSegment(sketch, "E96.1.1.23", {"start": v(75.38, 77.5) * mm, "end": v(70.5, 77.5) * mm});
            skLineSegment(sketch, "E96.1.1.24", {"start": v(25.12, 42.5) * mm, "end": v(30, 42.5) * mm});
            skPoint(sketch, "E96.1.1.25", {"position": v(51.75, 57.5) * mm});
            skPoint(sketch, "E96.1.1.26", {"position": v(65.5, 57.5) * mm});
            skPoint(sketch, "E96.1.1.27", {"position": v(51.75, 77.5) * mm});
            skPoint(sketch, "E96.1.1.28", {"position": v(48.75, 57.5) * mm});
            skPoint(sketch, "E96.1.1.29", {"position": v(50.25, 60) * mm});
            skLineSegment(sketch, "E96.1.1.30", {"start": v(48.75, 64.5) * mm, "end": v(48.75, 75.5) * mm});
            skLineSegment(sketch, "E96.1.1.31", {"start": v(46.75, 57.5) * mm, "end": v(37, 57.5) * mm});
            skLineSegment(sketch, "E96.1.1.32", {"start": v(46.75, 77.5) * mm, "end": v(37, 77.5) * mm});
            skLineSegment(sketch, "E96.1.1.33", {"start": v(46.75, 62.5) * mm, "end": v(37, 62.5) * mm});
            skPoint(sketch, "E96.1.1.34", {"position": v(80.25, 77.5) * mm});
            skLineSegment(sketch, "E96.1.1.35", {"start": v(75.38, 42.5) * mm, "end": v(70.5, 42.5) * mm});
            skPoint(sketch, "E96.1.1.36", {"position": v(68.5, 42.5) * mm});
            skPoint(sketch, "E96.1.1.37", {"position": v(48.75, 42.5) * mm});
            skPoint(sketch, "E96.1.1.38", {"position": v(20.25, 57.5) * mm});
            skPoint(sketch, "E96.1.1.39", {"position": v(48.75, 62.5) * mm});
            skLineSegment(sketch, "E96.1.1.40", {"start": v(32, 55.5) * mm, "end": v(32, 44.5) * mm});
            skPoint(sketch, "E96.1.1.41", {"position": v(68.5, 62.5) * mm});
            skPoint(sketch, "E96.1.1.42", {"position": v(68.5, 57.5) * mm});
            skLineSegment(sketch, "E96.1.1.43", {"start": v(75.38, 62.5) * mm, "end": v(75.38, 57.5) * mm});
            skLineSegment(sketch, "E96.1.1.44", {"start": v(53.75, 42.5) * mm, "end": v(63.5, 42.5) * mm});
            skLineSegment(sketch, "E96.1.1.45", {"start": v(48.75, 55.5) * mm, "end": v(48.75, 44.5) * mm});
            skLineSegment(sketch, "E96.1.1.46", {"start": v(35, 55.5) * mm, "end": v(35, 44.5) * mm});
            skLineSegment(sketch, "E96.1.1.47", {"start": v(75.38, 82.5) * mm, "end": v(25.12, 82.5) * mm});
            skPoint(sketch, "E96.1.1.48", {"position": v(32, 62.5) * mm});
            skLineSegment(sketch, "E96.1.1.49", {"start": v(75.38, 62.5) * mm, "end": v(70.5, 62.5) * mm});
            skPoint(sketch, "E96.1.1.50", {"position": v(32, 57.5) * mm});
            skLineSegment(sketch, "E96.1.1.51", {"start": v(25.12, 57.5) * mm, "end": v(30, 57.5) * mm});
            skPoint(sketch, "E96.1.1.52", {"position": v(35, 57.5) * mm});
            skPoint(sketch, "E96.1.1.53", {"position": v(65.5, 77.5) * mm});
            skLineSegment(sketch, "E96.1.1.54", {"start": v(68.5, 55.5) * mm, "end": v(68.5, 44.5) * mm});
            skLineSegment(sketch, "E96.1.1.55", {"start": v(53.75, 57.5) * mm, "end": v(63.5, 57.5) * mm});
            skPoint(sketch, "E96.1.1.56", {"position": v(20.25, 42.5) * mm});
            skPoint(sketch, "E96.1.1.57", {"position": v(20.25, 77.5) * mm});
            skLineSegment(sketch, "E96.1.1.58", {"start": v(25.12, 77.5) * mm, "end": v(30, 77.5) * mm});
            skLineSegment(sketch, "E96.1.1.59", {"start": v(65.5, 55.5) * mm, "end": v(65.5, 44.5) * mm});
            skLineSegment(sketch, "E96.1.1.60", {"start": v(32, 64.5) * mm, "end": v(32, 75.5) * mm});
            skLineSegment(sketch, "E96.1.1.61", {"start": v(68.5, 64.5) * mm, "end": v(68.5, 75.5) * mm});
            skPoint(sketch, "E96.1.1.62", {"position": v(35, 42.5) * mm});
            skPoint(sketch, "E96.1.1.63", {"position": v(80.25, 57.5) * mm});
            skPoint(sketch, "E96.1.1.64", {"position": v(68.5, 77.5) * mm});
            skLineSegment(sketch, "E96.1.1.65", {"start": v(25.12, 62.5) * mm, "end": v(25.12, 57.5) * mm});
            skArc(sketch, "E96.1.1.66", {"start": v(37, 77.5) * mm, "mid": v(35.59, 76.91) * mm, "end": v(35, 75.5) * mm});
            skArc(sketch, "E96.1.1.67", {"start": v(32, 64.5) * mm, "mid": v(31.41, 63.09) * mm, "end": v(30, 62.5) * mm});
            skArc(sketch, "E96.1.1.68", {"start": v(35, 64.5) * mm, "mid": v(35.59, 63.09) * mm, "end": v(37, 62.5) * mm});
            skArc(sketch, "E96.1.1.69", {"start": v(63.5, 77.5) * mm, "mid": v(64.91, 76.91) * mm, "end": v(65.5, 75.5) * mm});
            skArc(sketch, "E96.1.1.70", {"start": v(65.5, 64.5) * mm, "mid": v(64.91, 63.09) * mm, "end": v(63.5, 62.5) * mm});
            skArc(sketch, "E96.1.1.71", {"start": v(48.75, 44.5) * mm, "mid": v(48.16, 43.09) * mm, "end": v(46.75, 42.5) * mm});
            skArc(sketch, "E96.1.1.72", {"start": v(53.75, 62.5) * mm, "mid": v(52.34, 63.09) * mm, "end": v(51.75, 64.5) * mm});
            skArc(sketch, "E96.1.1.73", {"start": v(51.75, 44.5) * mm, "mid": v(52.34, 43.09) * mm, "end": v(53.75, 42.5) * mm});
            skArc(sketch, "E96.1.1.74", {"start": v(46.75, 62.5) * mm, "mid": v(48.16, 63.09) * mm, "end": v(48.75, 64.5) * mm});
            skArc(sketch, "E96.1.1.75", {"start": v(32, 55.5) * mm, "mid": v(31.41, 56.91) * mm, "end": v(30, 57.5) * mm});
            skArc(sketch, "E96.1.1.76", {"start": v(48.75, 75.5) * mm, "mid": v(48.16, 76.91) * mm, "end": v(46.75, 77.5) * mm});
            skArc(sketch, "E96.1.1.77", {"start": v(46.75, 57.5) * mm, "mid": v(48.16, 56.91) * mm, "end": v(48.75, 55.5) * mm});
            skLineSegment(sketch, "E96.1.1.78", {"start": v(75.38, 82.5) * mm, "end": v(75.38, 77.5) * mm});
            skArc(sketch, "E96.1.1.79", {"start": v(63.5, 42.5) * mm, "mid": v(64.91, 43.09) * mm, "end": v(65.5, 44.5) * mm});
            skArc(sketch, "E96.1.1.80", {"start": v(53.75, 57.5) * mm, "mid": v(52.34, 56.91) * mm, "end": v(51.75, 55.5) * mm});
            skArc(sketch, "E96.1.1.81", {"start": v(51.75, 75.5) * mm, "mid": v(52.34, 76.91) * mm, "end": v(53.75, 77.5) * mm});
            skArc(sketch, "E96.1.1.82", {"start": v(68.5, 64.5) * mm, "mid": v(69.09, 63.09) * mm, "end": v(70.5, 62.5) * mm});
            skArc(sketch, "E96.1.1.83", {"start": v(68.5, 55.5) * mm, "mid": v(69.09, 56.91) * mm, "end": v(70.5, 57.5) * mm});
            skArc(sketch, "E96.1.1.84", {"start": v(70.5, 77.5) * mm, "mid": v(69.09, 76.91) * mm, "end": v(68.5, 75.5) * mm});
            skLineSegment(sketch, "E96.1.1.85", {"start": v(75.38, 42.5) * mm, "end": v(75.38, 37.5) * mm});
            skArc(sketch, "E96.1.1.86", {"start": v(35, 55.5) * mm, "mid": v(35.59, 56.91) * mm, "end": v(37, 57.5) * mm});
            skArc(sketch, "E96.1.1.87", {"start": v(65.5, 55.5) * mm, "mid": v(64.91, 56.91) * mm, "end": v(63.5, 57.5) * mm});
            skArc(sketch, "E96.1.1.88", {"start": v(37, 42.5) * mm, "mid": v(35.59, 43.09) * mm, "end": v(35, 44.5) * mm});
            skArc(sketch, "E96.1.1.89", {"start": v(30, 42.5) * mm, "mid": v(31.41, 43.09) * mm, "end": v(32, 44.5) * mm});
            skArc(sketch, "E96.1.1.90", {"start": v(70.5, 42.5) * mm, "mid": v(69.09, 43.09) * mm, "end": v(68.5, 44.5) * mm});
            skArc(sketch, "E96.1.1.91", {"start": v(30, 77.5) * mm, "mid": v(31.41, 76.91) * mm, "end": v(32, 75.5) * mm});
            skLineSegment(sketch, "E96.1.1.92", {"start": v(25.12, 42.5) * mm, "end": v(25.12, 37.5) * mm});
            skLineSegment(sketch, "E96.1.1.93", {"start": v(25.12, 82.5) * mm, "end": v(25.12, 77.5) * mm});
            skLineSegment(sketch, "E96.1.1.94", {"start": v(25.12, 82.5) * mm, "end": v(25.12, 77.5) * mm});
            skLineSegment(sketch, "E96.1.1.95", {"start": v(25.12, 42.5) * mm, "end": v(25.12, 37.5) * mm});
            skLineSegment(sketch, "E96.1.2.0", {"start": v(51.75, 115.5) * mm, "end": v(51.75, 104.5) * mm});
            skPoint(sketch, "E96.1.2.1", {"position": v(80.25, 122.5) * mm});
            skLineSegment(sketch, "E96.1.2.2", {"start": v(35, 124.5) * mm, "end": v(35, 135.5) * mm});
            skPoint(sketch, "E96.1.2.3", {"position": v(51.75, 122.5) * mm});
            skLineSegment(sketch, "E96.1.2.4", {"start": v(25.12, 122.5) * mm, "end": v(30, 122.5) * mm});
            skPoint(sketch, "E96.1.2.5", {"position": v(65.5, 122.5) * mm});
            skPoint(sketch, "E96.1.2.6", {"position": v(32, 137.5) * mm});
            skPoint(sketch, "E96.1.2.7", {"position": v(65.5, 102.5) * mm});
            skPoint(sketch, "E96.1.2.8", {"position": v(32, 102.5) * mm});
            skLineSegment(sketch, "E96.1.2.9", {"start": v(75.38, 97.5) * mm, "end": v(25.12, 97.5) * mm});
            skLineSegment(sketch, "E96.1.2.10", {"start": v(65.5, 124.5) * mm, "end": v(65.5, 135.5) * mm});
            skLineSegment(sketch, "E96.1.2.11", {"start": v(53.75, 122.5) * mm, "end": v(63.5, 122.5) * mm});
            skPoint(sketch, "E96.1.2.12", {"position": v(48.75, 137.5) * mm});
            skPoint(sketch, "E96.1.2.13", {"position": v(51.75, 102.5) * mm});
            skPoint(sketch, "E96.1.2.14", {"position": v(20.25, 122.5) * mm});
            skPoint(sketch, "E96.1.2.15", {"position": v(80.25, 102.5) * mm});
            skLineSegment(sketch, "E96.1.2.16", {"start": v(25.12, 122.5) * mm, "end": v(25.12, 117.5) * mm});
            skLineSegment(sketch, "E96.1.2.17", {"start": v(75.38, 117.5) * mm, "end": v(70.5, 117.5) * mm});
            skLineSegment(sketch, "E96.1.2.18", {"start": v(46.75, 102.5) * mm, "end": v(37, 102.5) * mm});
            skPoint(sketch, "E96.1.2.19", {"position": v(35, 122.5) * mm});
            skLineSegment(sketch, "E96.1.2.20", {"start": v(53.75, 137.5) * mm, "end": v(63.5, 137.5) * mm});
            skPoint(sketch, "E96.1.2.21", {"position": v(35, 137.5) * mm});
            skLineSegment(sketch, "E96.1.2.22", {"start": v(51.75, 124.5) * mm, "end": v(51.75, 135.5) * mm});
            skLineSegment(sketch, "E96.1.2.23", {"start": v(75.38, 137.5) * mm, "end": v(70.5, 137.5) * mm});
            skLineSegment(sketch, "E96.1.2.24", {"start": v(25.12, 102.5) * mm, "end": v(30, 102.5) * mm});
            skPoint(sketch, "E96.1.2.25", {"position": v(51.75, 117.5) * mm});
            skPoint(sketch, "E96.1.2.26", {"position": v(65.5, 117.5) * mm});
            skPoint(sketch, "E96.1.2.27", {"position": v(51.75, 137.5) * mm});
            skPoint(sketch, "E96.1.2.28", {"position": v(48.75, 117.5) * mm});
            skPoint(sketch, "E96.1.2.29", {"position": v(50.25, 120) * mm});
            skLineSegment(sketch, "E96.1.2.30", {"start": v(48.75, 124.5) * mm, "end": v(48.75, 135.5) * mm});
            skLineSegment(sketch, "E96.1.2.31", {"start": v(46.75, 117.5) * mm, "end": v(37, 117.5) * mm});
            skLineSegment(sketch, "E96.1.2.32", {"start": v(46.75, 137.5) * mm, "end": v(37, 137.5) * mm});
            skLineSegment(sketch, "E96.1.2.33", {"start": v(46.75, 122.5) * mm, "end": v(37, 122.5) * mm});
            skPoint(sketch, "E96.1.2.34", {"position": v(80.25, 137.5) * mm});
            skLineSegment(sketch, "E96.1.2.35", {"start": v(75.38, 102.5) * mm, "end": v(70.5, 102.5) * mm});
            skPoint(sketch, "E96.1.2.36", {"position": v(68.5, 102.5) * mm});
            skPoint(sketch, "E96.1.2.37", {"position": v(48.75, 102.5) * mm});
            skPoint(sketch, "E96.1.2.38", {"position": v(20.25, 117.5) * mm});
            skPoint(sketch, "E96.1.2.39", {"position": v(48.75, 122.5) * mm});
            skLineSegment(sketch, "E96.1.2.40", {"start": v(32, 115.5) * mm, "end": v(32, 104.5) * mm});
            skPoint(sketch, "E96.1.2.41", {"position": v(68.5, 122.5) * mm});
            skPoint(sketch, "E96.1.2.42", {"position": v(68.5, 117.5) * mm});
            skLineSegment(sketch, "E96.1.2.43", {"start": v(75.38, 122.5) * mm, "end": v(75.38, 117.5) * mm});
            skLineSegment(sketch, "E96.1.2.44", {"start": v(53.75, 102.5) * mm, "end": v(63.5, 102.5) * mm});
            skLineSegment(sketch, "E96.1.2.45", {"start": v(48.75, 115.5) * mm, "end": v(48.75, 104.5) * mm});
            skLineSegment(sketch, "E96.1.2.46", {"start": v(35, 115.5) * mm, "end": v(35, 104.5) * mm});
            skLineSegment(sketch, "E96.1.2.47", {"start": v(75.38, 142.5) * mm, "end": v(25.12, 142.5) * mm});
            skPoint(sketch, "E96.1.2.48", {"position": v(32, 122.5) * mm});
            skLineSegment(sketch, "E96.1.2.49", {"start": v(75.38, 122.5) * mm, "end": v(70.5, 122.5) * mm});
            skPoint(sketch, "E96.1.2.50", {"position": v(32, 117.5) * mm});
            skLineSegment(sketch, "E96.1.2.51", {"start": v(25.12, 117.5) * mm, "end": v(30, 117.5) * mm});
            skPoint(sketch, "E96.1.2.52", {"position": v(35, 117.5) * mm});
            skPoint(sketch, "E96.1.2.53", {"position": v(65.5, 137.5) * mm});
            skLineSegment(sketch, "E96.1.2.54", {"start": v(68.5, 115.5) * mm, "end": v(68.5, 104.5) * mm});
            skLineSegment(sketch, "E96.1.2.55", {"start": v(53.75, 117.5) * mm, "end": v(63.5, 117.5) * mm});
            skPoint(sketch, "E96.1.2.56", {"position": v(20.25, 102.5) * mm});
            skPoint(sketch, "E96.1.2.57", {"position": v(20.25, 137.5) * mm});
            skLineSegment(sketch, "E96.1.2.58", {"start": v(25.12, 137.5) * mm, "end": v(30, 137.5) * mm});
            skLineSegment(sketch, "E96.1.2.59", {"start": v(65.5, 115.5) * mm, "end": v(65.5, 104.5) * mm});
            skLineSegment(sketch, "E96.1.2.60", {"start": v(32, 124.5) * mm, "end": v(32, 135.5) * mm});
            skLineSegment(sketch, "E96.1.2.61", {"start": v(68.5, 124.5) * mm, "end": v(68.5, 135.5) * mm});
            skPoint(sketch, "E96.1.2.62", {"position": v(35, 102.5) * mm});
            skPoint(sketch, "E96.1.2.63", {"position": v(80.25, 117.5) * mm});
            skPoint(sketch, "E96.1.2.64", {"position": v(68.5, 137.5) * mm});
            skLineSegment(sketch, "E96.1.2.65", {"start": v(25.12, 122.5) * mm, "end": v(25.12, 117.5) * mm});
            skArc(sketch, "E96.1.2.66", {"start": v(37, 137.5) * mm, "mid": v(35.59, 136.91) * mm, "end": v(35, 135.5) * mm});
            skArc(sketch, "E96.1.2.67", {"start": v(32, 124.5) * mm, "mid": v(31.41, 123.09) * mm, "end": v(30, 122.5) * mm});
            skArc(sketch, "E96.1.2.68", {"start": v(35, 124.5) * mm, "mid": v(35.59, 123.09) * mm, "end": v(37, 122.5) * mm});
            skArc(sketch, "E96.1.2.69", {"start": v(63.5, 137.5) * mm, "mid": v(64.91, 136.91) * mm, "end": v(65.5, 135.5) * mm});
            skArc(sketch, "E96.1.2.70", {"start": v(65.5, 124.5) * mm, "mid": v(64.91, 123.09) * mm, "end": v(63.5, 122.5) * mm});
            skArc(sketch, "E96.1.2.71", {"start": v(48.75, 104.5) * mm, "mid": v(48.16, 103.09) * mm, "end": v(46.75, 102.5) * mm});
            skArc(sketch, "E96.1.2.72", {"start": v(53.75, 122.5) * mm, "mid": v(52.34, 123.09) * mm, "end": v(51.75, 124.5) * mm});
            skArc(sketch, "E96.1.2.73", {"start": v(51.75, 104.5) * mm, "mid": v(52.34, 103.09) * mm, "end": v(53.75, 102.5) * mm});
            skArc(sketch, "E96.1.2.74", {"start": v(46.75, 122.5) * mm, "mid": v(48.16, 123.09) * mm, "end": v(48.75, 124.5) * mm});
            skArc(sketch, "E96.1.2.75", {"start": v(32, 115.5) * mm, "mid": v(31.41, 116.91) * mm, "end": v(30, 117.5) * mm});
            skArc(sketch, "E96.1.2.76", {"start": v(48.75, 135.5) * mm, "mid": v(48.16, 136.91) * mm, "end": v(46.75, 137.5) * mm});
            skArc(sketch, "E96.1.2.77", {"start": v(46.75, 117.5) * mm, "mid": v(48.16, 116.91) * mm, "end": v(48.75, 115.5) * mm});
            skLineSegment(sketch, "E96.1.2.78", {"start": v(75.38, 142.5) * mm, "end": v(75.38, 137.5) * mm});
            skArc(sketch, "E96.1.2.79", {"start": v(63.5, 102.5) * mm, "mid": v(64.91, 103.09) * mm, "end": v(65.5, 104.5) * mm});
            skArc(sketch, "E96.1.2.80", {"start": v(53.75, 117.5) * mm, "mid": v(52.34, 116.91) * mm, "end": v(51.75, 115.5) * mm});
            skArc(sketch, "E96.1.2.81", {"start": v(51.75, 135.5) * mm, "mid": v(52.34, 136.91) * mm, "end": v(53.75, 137.5) * mm});
            skArc(sketch, "E96.1.2.82", {"start": v(68.5, 124.5) * mm, "mid": v(69.09, 123.09) * mm, "end": v(70.5, 122.5) * mm});
            skArc(sketch, "E96.1.2.83", {"start": v(68.5, 115.5) * mm, "mid": v(69.09, 116.91) * mm, "end": v(70.5, 117.5) * mm});
            skArc(sketch, "E96.1.2.84", {"start": v(70.5, 137.5) * mm, "mid": v(69.09, 136.91) * mm, "end": v(68.5, 135.5) * mm});
            skLineSegment(sketch, "E96.1.2.85", {"start": v(75.38, 102.5) * mm, "end": v(75.38, 97.5) * mm});
            skArc(sketch, "E96.1.2.86", {"start": v(35, 115.5) * mm, "mid": v(35.59, 116.91) * mm, "end": v(37, 117.5) * mm});
            skArc(sketch, "E96.1.2.87", {"start": v(65.5, 115.5) * mm, "mid": v(64.91, 116.91) * mm, "end": v(63.5, 117.5) * mm});
            skArc(sketch, "E96.1.2.88", {"start": v(37, 102.5) * mm, "mid": v(35.59, 103.09) * mm, "end": v(35, 104.5) * mm});
            skArc(sketch, "E96.1.2.89", {"start": v(30, 102.5) * mm, "mid": v(31.41, 103.09) * mm, "end": v(32, 104.5) * mm});
            skArc(sketch, "E96.1.2.90", {"start": v(70.5, 102.5) * mm, "mid": v(69.09, 103.09) * mm, "end": v(68.5, 104.5) * mm});
            skArc(sketch, "E96.1.2.91", {"start": v(30, 137.5) * mm, "mid": v(31.41, 136.91) * mm, "end": v(32, 135.5) * mm});
            skLineSegment(sketch, "E96.1.2.92", {"start": v(25.12, 102.5) * mm, "end": v(25.12, 97.5) * mm});
            skLineSegment(sketch, "E96.1.2.93", {"start": v(25.12, 142.5) * mm, "end": v(25.12, 137.5) * mm});
            skLineSegment(sketch, "E96.1.2.94", {"start": v(25.12, 142.5) * mm, "end": v(25.12, 137.5) * mm});
            skLineSegment(sketch, "E96.1.2.95", {"start": v(25.12, 102.5) * mm, "end": v(25.12, 97.5) * mm});
            skLineSegment(sketch, "E96.2.0.0", {"start": v(102, -4.5) * mm, "end": v(102, -15.5) * mm});
            skPoint(sketch, "E96.2.0.1", {"position": v(130.5, 2.5) * mm});
            skLineSegment(sketch, "E96.2.0.2", {"start": v(85.25, 4.5) * mm, "end": v(85.25, 15.5) * mm});
            skPoint(sketch, "E96.2.0.3", {"position": v(102, 2.5) * mm});
            skLineSegment(sketch, "E96.2.0.4", {"start": v(75.38, 2.5) * mm, "end": v(80.25, 2.5) * mm});
            skPoint(sketch, "E96.2.0.5", {"position": v(115.75, 2.5) * mm});
            skPoint(sketch, "E96.2.0.6", {"position": v(82.25, 17.5) * mm});
            skPoint(sketch, "E96.2.0.7", {"position": v(115.75, -17.5) * mm});
            skPoint(sketch, "E96.2.0.8", {"position": v(82.25, -17.5) * mm});
            skLineSegment(sketch, "E96.2.0.9", {"start": v(125.63, -22.5) * mm, "end": v(75.38, -22.5) * mm});
            skLineSegment(sketch, "E96.2.0.10", {"start": v(115.75, 4.5) * mm, "end": v(115.75, 15.5) * mm});
            skLineSegment(sketch, "E96.2.0.11", {"start": v(104, 2.5) * mm, "end": v(113.75, 2.5) * mm});
            skPoint(sketch, "E96.2.0.12", {"position": v(99, 17.5) * mm});
            skPoint(sketch, "E96.2.0.13", {"position": v(102, -17.5) * mm});
            skPoint(sketch, "E96.2.0.14", {"position": v(70.5, 2.5) * mm});
            skPoint(sketch, "E96.2.0.15", {"position": v(130.5, -17.5) * mm});
            skLineSegment(sketch, "E96.2.0.16", {"start": v(75.38, 2.5) * mm, "end": v(75.38, -2.5) * mm});
            skLineSegment(sketch, "E96.2.0.17", {"start": v(125.63, -2.5) * mm, "end": v(120.75, -2.5) * mm});
            skLineSegment(sketch, "E96.2.0.18", {"start": v(97, -17.5) * mm, "end": v(87.25, -17.5) * mm});
            skPoint(sketch, "E96.2.0.19", {"position": v(85.25, 2.5) * mm});
            skLineSegment(sketch, "E96.2.0.20", {"start": v(104, 17.5) * mm, "end": v(113.75, 17.5) * mm});
            skPoint(sketch, "E96.2.0.21", {"position": v(85.25, 17.5) * mm});
            skLineSegment(sketch, "E96.2.0.22", {"start": v(102, 4.5) * mm, "end": v(102, 15.5) * mm});
            skLineSegment(sketch, "E96.2.0.23", {"start": v(125.63, 17.5) * mm, "end": v(120.75, 17.5) * mm});
            skLineSegment(sketch, "E96.2.0.24", {"start": v(75.38, -17.5) * mm, "end": v(80.25, -17.5) * mm});
            skPoint(sketch, "E96.2.0.25", {"position": v(102, -2.5) * mm});
            skPoint(sketch, "E96.2.0.26", {"position": v(115.75, -2.5) * mm});
            skPoint(sketch, "E96.2.0.27", {"position": v(102, 17.5) * mm});
            skPoint(sketch, "E96.2.0.28", {"position": v(99, -2.5) * mm});
            skPoint(sketch, "E96.2.0.29", {"position": v(100.5, 0) * mm});
            skLineSegment(sketch, "E96.2.0.30", {"start": v(99, 4.5) * mm, "end": v(99, 15.5) * mm});
            skLineSegment(sketch, "E96.2.0.31", {"start": v(97, -2.5) * mm, "end": v(87.25, -2.5) * mm});
            skLineSegment(sketch, "E96.2.0.32", {"start": v(97, 17.5) * mm, "end": v(87.25, 17.5) * mm});
            skLineSegment(sketch, "E96.2.0.33", {"start": v(97, 2.5) * mm, "end": v(87.25, 2.5) * mm});
            skPoint(sketch, "E96.2.0.34", {"position": v(130.5, 17.5) * mm});
            skLineSegment(sketch, "E96.2.0.35", {"start": v(125.63, -17.5) * mm, "end": v(120.75, -17.5) * mm});
            skPoint(sketch, "E96.2.0.36", {"position": v(118.75, -17.5) * mm});
            skPoint(sketch, "E96.2.0.37", {"position": v(99, -17.5) * mm});
            skPoint(sketch, "E96.2.0.38", {"position": v(70.5, -2.5) * mm});
            skPoint(sketch, "E96.2.0.39", {"position": v(99, 2.5) * mm});
            skLineSegment(sketch, "E96.2.0.40", {"start": v(82.25, -4.5) * mm, "end": v(82.25, -15.5) * mm});
            skPoint(sketch, "E96.2.0.41", {"position": v(118.75, 2.5) * mm});
            skPoint(sketch, "E96.2.0.42", {"position": v(118.75, -2.5) * mm});
            skLineSegment(sketch, "E96.2.0.43", {"start": v(125.63, 2.5) * mm, "end": v(125.63, -2.5) * mm});
            skLineSegment(sketch, "E96.2.0.44", {"start": v(104, -17.5) * mm, "end": v(113.75, -17.5) * mm});
            skLineSegment(sketch, "E96.2.0.45", {"start": v(99, -4.5) * mm, "end": v(99, -15.5) * mm});
            skLineSegment(sketch, "E96.2.0.46", {"start": v(85.25, -4.5) * mm, "end": v(85.25, -15.5) * mm});
            skLineSegment(sketch, "E96.2.0.47", {"start": v(125.63, 22.5) * mm, "end": v(75.38, 22.5) * mm});
            skPoint(sketch, "E96.2.0.48", {"position": v(82.25, 2.5) * mm});
            skLineSegment(sketch, "E96.2.0.49", {"start": v(125.63, 2.5) * mm, "end": v(120.75, 2.5) * mm});
            skPoint(sketch, "E96.2.0.50", {"position": v(82.25, -2.5) * mm});
            skLineSegment(sketch, "E96.2.0.51", {"start": v(75.38, -2.5) * mm, "end": v(80.25, -2.5) * mm});
            skPoint(sketch, "E96.2.0.52", {"position": v(85.25, -2.5) * mm});
            skPoint(sketch, "E96.2.0.53", {"position": v(115.75, 17.5) * mm});
            skLineSegment(sketch, "E96.2.0.54", {"start": v(118.75, -4.5) * mm, "end": v(118.75, -15.5) * mm});
            skLineSegment(sketch, "E96.2.0.55", {"start": v(104, -2.5) * mm, "end": v(113.75, -2.5) * mm});
            skPoint(sketch, "E96.2.0.56", {"position": v(70.5, -17.5) * mm});
            skPoint(sketch, "E96.2.0.57", {"position": v(70.5, 17.5) * mm});
            skLineSegment(sketch, "E96.2.0.58", {"start": v(75.38, 17.5) * mm, "end": v(80.25, 17.5) * mm});
            skLineSegment(sketch, "E96.2.0.59", {"start": v(115.75, -4.5) * mm, "end": v(115.75, -15.5) * mm});
            skLineSegment(sketch, "E96.2.0.60", {"start": v(82.25, 4.5) * mm, "end": v(82.25, 15.5) * mm});
            skLineSegment(sketch, "E96.2.0.61", {"start": v(118.75, 4.5) * mm, "end": v(118.75, 15.5) * mm});
            skPoint(sketch, "E96.2.0.62", {"position": v(85.25, -17.5) * mm});
            skPoint(sketch, "E96.2.0.63", {"position": v(130.5, -2.5) * mm});
            skPoint(sketch, "E96.2.0.64", {"position": v(118.75, 17.5) * mm});
            skLineSegment(sketch, "E96.2.0.65", {"start": v(75.38, 2.5) * mm, "end": v(75.38, -2.5) * mm});
            skArc(sketch, "E96.2.0.66", {"start": v(87.25, 17.5) * mm, "mid": v(85.84, 16.91) * mm, "end": v(85.25, 15.5) * mm});
            skArc(sketch, "E96.2.0.67", {"start": v(82.25, 4.5) * mm, "mid": v(81.66, 3.09) * mm, "end": v(80.25, 2.5) * mm});
            skArc(sketch, "E96.2.0.68", {"start": v(85.25, 4.5) * mm, "mid": v(85.84, 3.09) * mm, "end": v(87.25, 2.5) * mm});
            skArc(sketch, "E96.2.0.69", {"start": v(113.75, 17.5) * mm, "mid": v(115.16, 16.91) * mm, "end": v(115.75, 15.5) * mm});
            skArc(sketch, "E96.2.0.70", {"start": v(115.75, 4.5) * mm, "mid": v(115.16, 3.09) * mm, "end": v(113.75, 2.5) * mm});
            skArc(sketch, "E96.2.0.71", {"start": v(99, -15.5) * mm, "mid": v(98.41, -16.91) * mm, "end": v(97, -17.5) * mm});
            skArc(sketch, "E96.2.0.72", {"start": v(104, 2.5) * mm, "mid": v(102.59, 3.09) * mm, "end": v(102, 4.5) * mm});
            skArc(sketch, "E96.2.0.73", {"start": v(102, -15.5) * mm, "mid": v(102.59, -16.91) * mm, "end": v(104, -17.5) * mm});
            skArc(sketch, "E96.2.0.74", {"start": v(97, 2.5) * mm, "mid": v(98.41, 3.09) * mm, "end": v(99, 4.5) * mm});
            skArc(sketch, "E96.2.0.75", {"start": v(82.25, -4.5) * mm, "mid": v(81.66, -3.09) * mm, "end": v(80.25, -2.5) * mm});
            skArc(sketch, "E96.2.0.76", {"start": v(99, 15.5) * mm, "mid": v(98.41, 16.91) * mm, "end": v(97, 17.5) * mm});
            skArc(sketch, "E96.2.0.77", {"start": v(97, -2.5) * mm, "mid": v(98.41, -3.09) * mm, "end": v(99, -4.5) * mm});
            skLineSegment(sketch, "E96.2.0.78", {"start": v(125.63, 22.5) * mm, "end": v(125.63, 17.5) * mm});
            skArc(sketch, "E96.2.0.79", {"start": v(113.75, -17.5) * mm, "mid": v(115.16, -16.91) * mm, "end": v(115.75, -15.5) * mm});
            skArc(sketch, "E96.2.0.80", {"start": v(104, -2.5) * mm, "mid": v(102.59, -3.09) * mm, "end": v(102, -4.5) * mm});
            skArc(sketch, "E96.2.0.81", {"start": v(102, 15.5) * mm, "mid": v(102.59, 16.91) * mm, "end": v(104, 17.5) * mm});
            skArc(sketch, "E96.2.0.82", {"start": v(118.75, 4.5) * mm, "mid": v(119.34, 3.09) * mm, "end": v(120.75, 2.5) * mm});
            skArc(sketch, "E96.2.0.83", {"start": v(118.75, -4.5) * mm, "mid": v(119.34, -3.09) * mm, "end": v(120.75, -2.5) * mm});
            skArc(sketch, "E96.2.0.84", {"start": v(120.75, 17.5) * mm, "mid": v(119.34, 16.91) * mm, "end": v(118.75, 15.5) * mm});
            skLineSegment(sketch, "E96.2.0.85", {"start": v(125.63, -17.5) * mm, "end": v(125.63, -22.5) * mm});
            skArc(sketch, "E96.2.0.86", {"start": v(85.25, -4.5) * mm, "mid": v(85.84, -3.09) * mm, "end": v(87.25, -2.5) * mm});
            skArc(sketch, "E96.2.0.87", {"start": v(115.75, -4.5) * mm, "mid": v(115.16, -3.09) * mm, "end": v(113.75, -2.5) * mm});
            skArc(sketch, "E96.2.0.88", {"start": v(87.25, -17.5) * mm, "mid": v(85.84, -16.91) * mm, "end": v(85.25, -15.5) * mm});
            skArc(sketch, "E96.2.0.89", {"start": v(80.25, -17.5) * mm, "mid": v(81.66, -16.91) * mm, "end": v(82.25, -15.5) * mm});
            skArc(sketch, "E96.2.0.90", {"start": v(120.75, -17.5) * mm, "mid": v(119.34, -16.91) * mm, "end": v(118.75, -15.5) * mm});
            skArc(sketch, "E96.2.0.91", {"start": v(80.25, 17.5) * mm, "mid": v(81.66, 16.91) * mm, "end": v(82.25, 15.5) * mm});
            skLineSegment(sketch, "E96.2.0.92", {"start": v(75.38, -17.5) * mm, "end": v(75.38, -22.5) * mm});
            skLineSegment(sketch, "E96.2.0.93", {"start": v(75.38, 22.5) * mm, "end": v(75.38, 17.5) * mm});
            skLineSegment(sketch, "E96.2.0.94", {"start": v(75.38, 22.5) * mm, "end": v(75.38, 17.5) * mm});
            skLineSegment(sketch, "E96.2.0.95", {"start": v(75.38, -17.5) * mm, "end": v(75.38, -22.5) * mm});
            skLineSegment(sketch, "E96.2.1.0", {"start": v(102, 55.5) * mm, "end": v(102, 44.5) * mm});
            skPoint(sketch, "E96.2.1.1", {"position": v(130.5, 62.5) * mm});
            skLineSegment(sketch, "E96.2.1.2", {"start": v(85.25, 64.5) * mm, "end": v(85.25, 75.5) * mm});
            skPoint(sketch, "E96.2.1.3", {"position": v(102, 62.5) * mm});
            skLineSegment(sketch, "E96.2.1.4", {"start": v(75.38, 62.5) * mm, "end": v(80.25, 62.5) * mm});
            skPoint(sketch, "E96.2.1.5", {"position": v(115.75, 62.5) * mm});
            skPoint(sketch, "E96.2.1.6", {"position": v(82.25, 77.5) * mm});
            skPoint(sketch, "E96.2.1.7", {"position": v(115.75, 42.5) * mm});
            skPoint(sketch, "E96.2.1.8", {"position": v(82.25, 42.5) * mm});
            skLineSegment(sketch, "E96.2.1.9", {"start": v(125.63, 37.5) * mm, "end": v(75.38, 37.5) * mm});
            skLineSegment(sketch, "E96.2.1.10", {"start": v(115.75, 64.5) * mm, "end": v(115.75, 75.5) * mm});
            skLineSegment(sketch, "E96.2.1.11", {"start": v(104, 62.5) * mm, "end": v(113.75, 62.5) * mm});
            skPoint(sketch, "E96.2.1.12", {"position": v(99, 77.5) * mm});
            skPoint(sketch, "E96.2.1.13", {"position": v(102, 42.5) * mm});
            skPoint(sketch, "E96.2.1.14", {"position": v(70.5, 62.5) * mm});
            skPoint(sketch, "E96.2.1.15", {"position": v(130.5, 42.5) * mm});
            skLineSegment(sketch, "E96.2.1.16", {"start": v(75.38, 62.5) * mm, "end": v(75.38, 57.5) * mm});
            skLineSegment(sketch, "E96.2.1.17", {"start": v(125.63, 57.5) * mm, "end": v(120.75, 57.5) * mm});
            skLineSegment(sketch, "E96.2.1.18", {"start": v(97, 42.5) * mm, "end": v(87.25, 42.5) * mm});
            skPoint(sketch, "E96.2.1.19", {"position": v(85.25, 62.5) * mm});
            skLineSegment(sketch, "E96.2.1.20", {"start": v(104, 77.5) * mm, "end": v(113.75, 77.5) * mm});
            skPoint(sketch, "E96.2.1.21", {"position": v(85.25, 77.5) * mm});
            skLineSegment(sketch, "E96.2.1.22", {"start": v(102, 64.5) * mm, "end": v(102, 75.5) * mm});
            skLineSegment(sketch, "E96.2.1.23", {"start": v(125.63, 77.5) * mm, "end": v(120.75, 77.5) * mm});
            skLineSegment(sketch, "E96.2.1.24", {"start": v(75.38, 42.5) * mm, "end": v(80.25, 42.5) * mm});
            skPoint(sketch, "E96.2.1.25", {"position": v(102, 57.5) * mm});
            skPoint(sketch, "E96.2.1.26", {"position": v(115.75, 57.5) * mm});
            skPoint(sketch, "E96.2.1.27", {"position": v(102, 77.5) * mm});
            skPoint(sketch, "E96.2.1.28", {"position": v(99, 57.5) * mm});
            skPoint(sketch, "E96.2.1.29", {"position": v(100.5, 60) * mm});
            skLineSegment(sketch, "E96.2.1.30", {"start": v(99, 64.5) * mm, "end": v(99, 75.5) * mm});
            skLineSegment(sketch, "E96.2.1.31", {"start": v(97, 57.5) * mm, "end": v(87.25, 57.5) * mm});
            skLineSegment(sketch, "E96.2.1.32", {"start": v(97, 77.5) * mm, "end": v(87.25, 77.5) * mm});
            skLineSegment(sketch, "E96.2.1.33", {"start": v(97, 62.5) * mm, "end": v(87.25, 62.5) * mm});
            skPoint(sketch, "E96.2.1.34", {"position": v(130.5, 77.5) * mm});
            skLineSegment(sketch, "E96.2.1.35", {"start": v(125.63, 42.5) * mm, "end": v(120.75, 42.5) * mm});
            skPoint(sketch, "E96.2.1.36", {"position": v(118.75, 42.5) * mm});
            skPoint(sketch, "E96.2.1.37", {"position": v(99, 42.5) * mm});
            skPoint(sketch, "E96.2.1.38", {"position": v(70.5, 57.5) * mm});
            skPoint(sketch, "E96.2.1.39", {"position": v(99, 62.5) * mm});
            skLineSegment(sketch, "E96.2.1.40", {"start": v(82.25, 55.5) * mm, "end": v(82.25, 44.5) * mm});
            skPoint(sketch, "E96.2.1.41", {"position": v(118.75, 62.5) * mm});
            skPoint(sketch, "E96.2.1.42", {"position": v(118.75, 57.5) * mm});
            skLineSegment(sketch, "E96.2.1.43", {"start": v(125.63, 62.5) * mm, "end": v(125.63, 57.5) * mm});
            skLineSegment(sketch, "E96.2.1.44", {"start": v(104, 42.5) * mm, "end": v(113.75, 42.5) * mm});
            skLineSegment(sketch, "E96.2.1.45", {"start": v(99, 55.5) * mm, "end": v(99, 44.5) * mm});
            skLineSegment(sketch, "E96.2.1.46", {"start": v(85.25, 55.5) * mm, "end": v(85.25, 44.5) * mm});
            skLineSegment(sketch, "E96.2.1.47", {"start": v(125.63, 82.5) * mm, "end": v(75.38, 82.5) * mm});
            skPoint(sketch, "E96.2.1.48", {"position": v(82.25, 62.5) * mm});
            skLineSegment(sketch, "E96.2.1.49", {"start": v(125.63, 62.5) * mm, "end": v(120.75, 62.5) * mm});
            skPoint(sketch, "E96.2.1.50", {"position": v(82.25, 57.5) * mm});
            skLineSegment(sketch, "E96.2.1.51", {"start": v(75.38, 57.5) * mm, "end": v(80.25, 57.5) * mm});
            skPoint(sketch, "E96.2.1.52", {"position": v(85.25, 57.5) * mm});
            skPoint(sketch, "E96.2.1.53", {"position": v(115.75, 77.5) * mm});
            skLineSegment(sketch, "E96.2.1.54", {"start": v(118.75, 55.5) * mm, "end": v(118.75, 44.5) * mm});
            skLineSegment(sketch, "E96.2.1.55", {"start": v(104, 57.5) * mm, "end": v(113.75, 57.5) * mm});
            skPoint(sketch, "E96.2.1.56", {"position": v(70.5, 42.5) * mm});
            skPoint(sketch, "E96.2.1.57", {"position": v(70.5, 77.5) * mm});
            skLineSegment(sketch, "E96.2.1.58", {"start": v(75.38, 77.5) * mm, "end": v(80.25, 77.5) * mm});
            skLineSegment(sketch, "E96.2.1.59", {"start": v(115.75, 55.5) * mm, "end": v(115.75, 44.5) * mm});
            skLineSegment(sketch, "E96.2.1.60", {"start": v(82.25, 64.5) * mm, "end": v(82.25, 75.5) * mm});
            skLineSegment(sketch, "E96.2.1.61", {"start": v(118.75, 64.5) * mm, "end": v(118.75, 75.5) * mm});
            skPoint(sketch, "E96.2.1.62", {"position": v(85.25, 42.5) * mm});
            skPoint(sketch, "E96.2.1.63", {"position": v(130.5, 57.5) * mm});
            skPoint(sketch, "E96.2.1.64", {"position": v(118.75, 77.5) * mm});
            skLineSegment(sketch, "E96.2.1.65", {"start": v(75.38, 62.5) * mm, "end": v(75.38, 57.5) * mm});
            skArc(sketch, "E96.2.1.66", {"start": v(87.25, 77.5) * mm, "mid": v(85.84, 76.91) * mm, "end": v(85.25, 75.5) * mm});
            skArc(sketch, "E96.2.1.67", {"start": v(82.25, 64.5) * mm, "mid": v(81.66, 63.09) * mm, "end": v(80.25, 62.5) * mm});
            skArc(sketch, "E96.2.1.68", {"start": v(85.25, 64.5) * mm, "mid": v(85.84, 63.09) * mm, "end": v(87.25, 62.5) * mm});
            skArc(sketch, "E96.2.1.69", {"start": v(113.75, 77.5) * mm, "mid": v(115.16, 76.91) * mm, "end": v(115.75, 75.5) * mm});
            skArc(sketch, "E96.2.1.70", {"start": v(115.75, 64.5) * mm, "mid": v(115.16, 63.09) * mm, "end": v(113.75, 62.5) * mm});
            skArc(sketch, "E96.2.1.71", {"start": v(99, 44.5) * mm, "mid": v(98.41, 43.09) * mm, "end": v(97, 42.5) * mm});
            skArc(sketch, "E96.2.1.72", {"start": v(104, 62.5) * mm, "mid": v(102.59, 63.09) * mm, "end": v(102, 64.5) * mm});
            skArc(sketch, "E96.2.1.73", {"start": v(102, 44.5) * mm, "mid": v(102.59, 43.09) * mm, "end": v(104, 42.5) * mm});
            skArc(sketch, "E96.2.1.74", {"start": v(97, 62.5) * mm, "mid": v(98.41, 63.09) * mm, "end": v(99, 64.5) * mm});
            skArc(sketch, "E96.2.1.75", {"start": v(82.25, 55.5) * mm, "mid": v(81.66, 56.91) * mm, "end": v(80.25, 57.5) * mm});
            skArc(sketch, "E96.2.1.76", {"start": v(99, 75.5) * mm, "mid": v(98.41, 76.91) * mm, "end": v(97, 77.5) * mm});
            skArc(sketch, "E96.2.1.77", {"start": v(97, 57.5) * mm, "mid": v(98.41, 56.91) * mm, "end": v(99, 55.5) * mm});
            skLineSegment(sketch, "E96.2.1.78", {"start": v(125.63, 82.5) * mm, "end": v(125.63, 77.5) * mm});
            skArc(sketch, "E96.2.1.79", {"start": v(113.75, 42.5) * mm, "mid": v(115.16, 43.09) * mm, "end": v(115.75, 44.5) * mm});
            skArc(sketch, "E96.2.1.80", {"start": v(104, 57.5) * mm, "mid": v(102.59, 56.91) * mm, "end": v(102, 55.5) * mm});
            skArc(sketch, "E96.2.1.81", {"start": v(102, 75.5) * mm, "mid": v(102.59, 76.91) * mm, "end": v(104, 77.5) * mm});
            skArc(sketch, "E96.2.1.82", {"start": v(118.75, 64.5) * mm, "mid": v(119.34, 63.09) * mm, "end": v(120.75, 62.5) * mm});
            skArc(sketch, "E96.2.1.83", {"start": v(118.75, 55.5) * mm, "mid": v(119.34, 56.91) * mm, "end": v(120.75, 57.5) * mm});
            skArc(sketch, "E96.2.1.84", {"start": v(120.75, 77.5) * mm, "mid": v(119.34, 76.91) * mm, "end": v(118.75, 75.5) * mm});
            skLineSegment(sketch, "E96.2.1.85", {"start": v(125.63, 42.5) * mm, "end": v(125.63, 37.5) * mm});
            skArc(sketch, "E96.2.1.86", {"start": v(85.25, 55.5) * mm, "mid": v(85.84, 56.91) * mm, "end": v(87.25, 57.5) * mm});
            skArc(sketch, "E96.2.1.87", {"start": v(115.75, 55.5) * mm, "mid": v(115.16, 56.91) * mm, "end": v(113.75, 57.5) * mm});
            skArc(sketch, "E96.2.1.88", {"start": v(87.25, 42.5) * mm, "mid": v(85.84, 43.09) * mm, "end": v(85.25, 44.5) * mm});
            skArc(sketch, "E96.2.1.89", {"start": v(80.25, 42.5) * mm, "mid": v(81.66, 43.09) * mm, "end": v(82.25, 44.5) * mm});
            skArc(sketch, "E96.2.1.90", {"start": v(120.75, 42.5) * mm, "mid": v(119.34, 43.09) * mm, "end": v(118.75, 44.5) * mm});
            skArc(sketch, "E96.2.1.91", {"start": v(80.25, 77.5) * mm, "mid": v(81.66, 76.91) * mm, "end": v(82.25, 75.5) * mm});
            skLineSegment(sketch, "E96.2.1.92", {"start": v(75.38, 42.5) * mm, "end": v(75.38, 37.5) * mm});
            skLineSegment(sketch, "E96.2.1.93", {"start": v(75.38, 82.5) * mm, "end": v(75.38, 77.5) * mm});
            skLineSegment(sketch, "E96.2.1.94", {"start": v(75.38, 82.5) * mm, "end": v(75.38, 77.5) * mm});
            skLineSegment(sketch, "E96.2.1.95", {"start": v(75.38, 42.5) * mm, "end": v(75.38, 37.5) * mm});
            skLineSegment(sketch, "E96.2.2.0", {"start": v(102, 115.5) * mm, "end": v(102, 104.5) * mm});
            skPoint(sketch, "E96.2.2.1", {"position": v(130.5, 122.5) * mm});
            skLineSegment(sketch, "E96.2.2.2", {"start": v(85.25, 124.5) * mm, "end": v(85.25, 135.5) * mm});
            skPoint(sketch, "E96.2.2.3", {"position": v(102, 122.5) * mm});
            skLineSegment(sketch, "E96.2.2.4", {"start": v(75.38, 122.5) * mm, "end": v(80.25, 122.5) * mm});
            skPoint(sketch, "E96.2.2.5", {"position": v(115.75, 122.5) * mm});
            skPoint(sketch, "E96.2.2.6", {"position": v(82.25, 137.5) * mm});
            skPoint(sketch, "E96.2.2.7", {"position": v(115.75, 102.5) * mm});
            skPoint(sketch, "E96.2.2.8", {"position": v(82.25, 102.5) * mm});
            skLineSegment(sketch, "E96.2.2.9", {"start": v(125.63, 97.5) * mm, "end": v(75.38, 97.5) * mm});
            skLineSegment(sketch, "E96.2.2.10", {"start": v(115.75, 124.5) * mm, "end": v(115.75, 135.5) * mm});
            skLineSegment(sketch, "E96.2.2.11", {"start": v(104, 122.5) * mm, "end": v(113.75, 122.5) * mm});
            skPoint(sketch, "E96.2.2.12", {"position": v(99, 137.5) * mm});
            skPoint(sketch, "E96.2.2.13", {"position": v(102, 102.5) * mm});
            skPoint(sketch, "E96.2.2.14", {"position": v(70.5, 122.5) * mm});
            skPoint(sketch, "E96.2.2.15", {"position": v(130.5, 102.5) * mm});
            skLineSegment(sketch, "E96.2.2.16", {"start": v(75.38, 122.5) * mm, "end": v(75.38, 117.5) * mm});
            skLineSegment(sketch, "E96.2.2.17", {"start": v(125.63, 117.5) * mm, "end": v(120.75, 117.5) * mm});
            skLineSegment(sketch, "E96.2.2.18", {"start": v(97, 102.5) * mm, "end": v(87.25, 102.5) * mm});
            skPoint(sketch, "E96.2.2.19", {"position": v(85.25, 122.5) * mm});
            skLineSegment(sketch, "E96.2.2.20", {"start": v(104, 137.5) * mm, "end": v(113.75, 137.5) * mm});
            skPoint(sketch, "E96.2.2.21", {"position": v(85.25, 137.5) * mm});
            skLineSegment(sketch, "E96.2.2.22", {"start": v(102, 124.5) * mm, "end": v(102, 135.5) * mm});
            skLineSegment(sketch, "E96.2.2.23", {"start": v(125.63, 137.5) * mm, "end": v(120.75, 137.5) * mm});
            skLineSegment(sketch, "E96.2.2.24", {"start": v(75.38, 102.5) * mm, "end": v(80.25, 102.5) * mm});
            skPoint(sketch, "E96.2.2.25", {"position": v(102, 117.5) * mm});
            skPoint(sketch, "E96.2.2.26", {"position": v(115.75, 117.5) * mm});
            skPoint(sketch, "E96.2.2.27", {"position": v(102, 137.5) * mm});
            skPoint(sketch, "E96.2.2.28", {"position": v(99, 117.5) * mm});
            skPoint(sketch, "E96.2.2.29", {"position": v(100.5, 120) * mm});
            skLineSegment(sketch, "E96.2.2.30", {"start": v(99, 124.5) * mm, "end": v(99, 135.5) * mm});
            skLineSegment(sketch, "E96.2.2.31", {"start": v(97, 117.5) * mm, "end": v(87.25, 117.5) * mm});
            skLineSegment(sketch, "E96.2.2.32", {"start": v(97, 137.5) * mm, "end": v(87.25, 137.5) * mm});
            skLineSegment(sketch, "E96.2.2.33", {"start": v(97, 122.5) * mm, "end": v(87.25, 122.5) * mm});
            skPoint(sketch, "E96.2.2.34", {"position": v(130.5, 137.5) * mm});
            skLineSegment(sketch, "E96.2.2.35", {"start": v(125.63, 102.5) * mm, "end": v(120.75, 102.5) * mm});
            skPoint(sketch, "E96.2.2.36", {"position": v(118.75, 102.5) * mm});
            skPoint(sketch, "E96.2.2.37", {"position": v(99, 102.5) * mm});
            skPoint(sketch, "E96.2.2.38", {"position": v(70.5, 117.5) * mm});
            skPoint(sketch, "E96.2.2.39", {"position": v(99, 122.5) * mm});
            skLineSegment(sketch, "E96.2.2.40", {"start": v(82.25, 115.5) * mm, "end": v(82.25, 104.5) * mm});
            skPoint(sketch, "E96.2.2.41", {"position": v(118.75, 122.5) * mm});
            skPoint(sketch, "E96.2.2.42", {"position": v(118.75, 117.5) * mm});
            skLineSegment(sketch, "E96.2.2.43", {"start": v(125.63, 122.5) * mm, "end": v(125.63, 117.5) * mm});
            skLineSegment(sketch, "E96.2.2.44", {"start": v(104, 102.5) * mm, "end": v(113.75, 102.5) * mm});
            skLineSegment(sketch, "E96.2.2.45", {"start": v(99, 115.5) * mm, "end": v(99, 104.5) * mm});
            skLineSegment(sketch, "E96.2.2.46", {"start": v(85.25, 115.5) * mm, "end": v(85.25, 104.5) * mm});
            skLineSegment(sketch, "E96.2.2.47", {"start": v(125.63, 142.5) * mm, "end": v(75.38, 142.5) * mm});
            skPoint(sketch, "E96.2.2.48", {"position": v(82.25, 122.5) * mm});
            skLineSegment(sketch, "E96.2.2.49", {"start": v(125.63, 122.5) * mm, "end": v(120.75, 122.5) * mm});
            skPoint(sketch, "E96.2.2.50", {"position": v(82.25, 117.5) * mm});
            skLineSegment(sketch, "E96.2.2.51", {"start": v(75.38, 117.5) * mm, "end": v(80.25, 117.5) * mm});
            skPoint(sketch, "E96.2.2.52", {"position": v(85.25, 117.5) * mm});
            skPoint(sketch, "E96.2.2.53", {"position": v(115.75, 137.5) * mm});
            skLineSegment(sketch, "E96.2.2.54", {"start": v(118.75, 115.5) * mm, "end": v(118.75, 104.5) * mm});
            skLineSegment(sketch, "E96.2.2.55", {"start": v(104, 117.5) * mm, "end": v(113.75, 117.5) * mm});
            skPoint(sketch, "E96.2.2.56", {"position": v(70.5, 102.5) * mm});
            skPoint(sketch, "E96.2.2.57", {"position": v(70.5, 137.5) * mm});
            skLineSegment(sketch, "E96.2.2.58", {"start": v(75.38, 137.5) * mm, "end": v(80.25, 137.5) * mm});
            skLineSegment(sketch, "E96.2.2.59", {"start": v(115.75, 115.5) * mm, "end": v(115.75, 104.5) * mm});
            skLineSegment(sketch, "E96.2.2.60", {"start": v(82.25, 124.5) * mm, "end": v(82.25, 135.5) * mm});
            skLineSegment(sketch, "E96.2.2.61", {"start": v(118.75, 124.5) * mm, "end": v(118.75, 135.5) * mm});
            skPoint(sketch, "E96.2.2.62", {"position": v(85.25, 102.5) * mm});
            skPoint(sketch, "E96.2.2.63", {"position": v(130.5, 117.5) * mm});
            skPoint(sketch, "E96.2.2.64", {"position": v(118.75, 137.5) * mm});
            skLineSegment(sketch, "E96.2.2.65", {"start": v(75.38, 122.5) * mm, "end": v(75.38, 117.5) * mm});
            skArc(sketch, "E96.2.2.66", {"start": v(87.25, 137.5) * mm, "mid": v(85.84, 136.91) * mm, "end": v(85.25, 135.5) * mm});
            skArc(sketch, "E96.2.2.67", {"start": v(82.25, 124.5) * mm, "mid": v(81.66, 123.09) * mm, "end": v(80.25, 122.5) * mm});
            skArc(sketch, "E96.2.2.68", {"start": v(85.25, 124.5) * mm, "mid": v(85.84, 123.09) * mm, "end": v(87.25, 122.5) * mm});
            skArc(sketch, "E96.2.2.69", {"start": v(113.75, 137.5) * mm, "mid": v(115.16, 136.91) * mm, "end": v(115.75, 135.5) * mm});
            skArc(sketch, "E96.2.2.70", {"start": v(115.75, 124.5) * mm, "mid": v(115.16, 123.09) * mm, "end": v(113.75, 122.5) * mm});
            skArc(sketch, "E96.2.2.71", {"start": v(99, 104.5) * mm, "mid": v(98.41, 103.09) * mm, "end": v(97, 102.5) * mm});
            skArc(sketch, "E96.2.2.72", {"start": v(104, 122.5) * mm, "mid": v(102.59, 123.09) * mm, "end": v(102, 124.5) * mm});
            skArc(sketch, "E96.2.2.73", {"start": v(102, 104.5) * mm, "mid": v(102.59, 103.09) * mm, "end": v(104, 102.5) * mm});
            skArc(sketch, "E96.2.2.74", {"start": v(97, 122.5) * mm, "mid": v(98.41, 123.09) * mm, "end": v(99, 124.5) * mm});
            skArc(sketch, "E96.2.2.75", {"start": v(82.25, 115.5) * mm, "mid": v(81.66, 116.91) * mm, "end": v(80.25, 117.5) * mm});
            skArc(sketch, "E96.2.2.76", {"start": v(99, 135.5) * mm, "mid": v(98.41, 136.91) * mm, "end": v(97, 137.5) * mm});
            skArc(sketch, "E96.2.2.77", {"start": v(97, 117.5) * mm, "mid": v(98.41, 116.91) * mm, "end": v(99, 115.5) * mm});
            skLineSegment(sketch, "E96.2.2.78", {"start": v(125.63, 142.5) * mm, "end": v(125.63, 137.5) * mm});
            skArc(sketch, "E96.2.2.79", {"start": v(113.75, 102.5) * mm, "mid": v(115.16, 103.09) * mm, "end": v(115.75, 104.5) * mm});
            skArc(sketch, "E96.2.2.80", {"start": v(104, 117.5) * mm, "mid": v(102.59, 116.91) * mm, "end": v(102, 115.5) * mm});
            skArc(sketch, "E96.2.2.81", {"start": v(102, 135.5) * mm, "mid": v(102.59, 136.91) * mm, "end": v(104, 137.5) * mm});
            skArc(sketch, "E96.2.2.82", {"start": v(118.75, 124.5) * mm, "mid": v(119.34, 123.09) * mm, "end": v(120.75, 122.5) * mm});
            skArc(sketch, "E96.2.2.83", {"start": v(118.75, 115.5) * mm, "mid": v(119.34, 116.91) * mm, "end": v(120.75, 117.5) * mm});
            skArc(sketch, "E96.2.2.84", {"start": v(120.75, 137.5) * mm, "mid": v(119.34, 136.91) * mm, "end": v(118.75, 135.5) * mm});
            skLineSegment(sketch, "E96.2.2.85", {"start": v(125.63, 102.5) * mm, "end": v(125.63, 97.5) * mm});
            skArc(sketch, "E96.2.2.86", {"start": v(85.25, 115.5) * mm, "mid": v(85.84, 116.91) * mm, "end": v(87.25, 117.5) * mm});
            skArc(sketch, "E96.2.2.87", {"start": v(115.75, 115.5) * mm, "mid": v(115.16, 116.91) * mm, "end": v(113.75, 117.5) * mm});
            skArc(sketch, "E96.2.2.88", {"start": v(87.25, 102.5) * mm, "mid": v(85.84, 103.09) * mm, "end": v(85.25, 104.5) * mm});
            skArc(sketch, "E96.2.2.89", {"start": v(80.25, 102.5) * mm, "mid": v(81.66, 103.09) * mm, "end": v(82.25, 104.5) * mm});
            skArc(sketch, "E96.2.2.90", {"start": v(120.75, 102.5) * mm, "mid": v(119.34, 103.09) * mm, "end": v(118.75, 104.5) * mm});
            skArc(sketch, "E96.2.2.91", {"start": v(80.25, 137.5) * mm, "mid": v(81.66, 136.91) * mm, "end": v(82.25, 135.5) * mm});
            skLineSegment(sketch, "E96.2.2.92", {"start": v(75.38, 102.5) * mm, "end": v(75.38, 97.5) * mm});
            skLineSegment(sketch, "E96.2.2.93", {"start": v(75.38, 142.5) * mm, "end": v(75.38, 137.5) * mm});
            skLineSegment(sketch, "E96.2.2.94", {"start": v(75.38, 142.5) * mm, "end": v(75.38, 137.5) * mm});
            skLineSegment(sketch, "E96.2.2.95", {"start": v(75.38, 102.5) * mm, "end": v(75.38, 97.5) * mm});
            skLineSegment(sketch, "E96.direction1", {"start": v(-30, -17.5) * mm, "end": v(20.25, -17.5) * mm, "construction": true});
            skLineSegment(sketch, "E96.direction2", {"start": v(-30, -17.5) * mm, "end": v(-30, 42.5) * mm, "construction": true});
            skSolve(sketch);
        }
        {
            var Q0;
            Q0=qSketchRegion(id+"F0",true);
            extrude(context, id + "F1", {"entities" : qUnion([Q0]), "depth" : .4 * mm});
        }
        {
            var Q0;
            Q0=qCreatedBy(makeId("Top.planeOp"),FACE);
            var sketch = newSketch(context, id + "F2", { "sketchPlane" : qUnion([Q0])});
            skLineSegment(sketch, "E97.bottom", {"start": v(169.38, 174.68) * mm, "end": v(-30.62, 174.68) * mm});
            skLineSegment(sketch, "E97.top", {"start": v(169.38, -25.32) * mm, "end": v(-30.62, -25.32) * mm});
            skLineSegment(sketch, "E97.left", {"start": v(169.38, 174.68) * mm, "end": v(169.38, -25.32) * mm});
            skLineSegment(sketch, "E97.right", {"start": v(-30.62, 174.68) * mm, "end": v(-30.62, -25.32) * mm});
            skSolve(sketch);
        }
        {
            var Q0;
            Q0=makeQuery(id+"F2.imprint","IMPRINT",FACE,{"disambiguationData":[TD([[makeQuery(id+"F2.imprint","IMPRINT",EDGE,{"derivedFrom":sQuery(id+"F2.wireOp",EDGE,"E97.bottom")}),1.0]])]});
            extrude(context, id + "F3", {"entities" : qUnion([Q0]), "oppositeDirection" : true, "depth" : 2 * mm});
        }
        {
            var Q0;
            Q0=makeQuery(id+"F3.opExtrude","SWEPT_BODY",BODY,{"disambiguationData":[OSD([sQuery(id+"F2.wireOp",EDGE,"E97.bottom"),sQuery(id+"F2.wireOp",EDGE,"E97.top"),sQuery(id+"F2.wireOp",EDGE,"E97.left"),sQuery(id+"F2.wireOp",EDGE,"E97.right")])]});
            transform(context, id + "F4", {"entities" : qUnion([Q0]), "transformType" : TransformType.TRANSLATION_3D, "dx" : 0 * mm, "dy" : 0 * mm, "dz" : .4 * mm, "makeCopy" : false});
        }
        {
            var Q0;
            Q0=makeQuery(id+"F1.opExtrude","SWEPT_BODY",BODY,{"disambiguationData":[OSD([sQuery(id+"F0.wireOp",EDGE,"E96.1.0.0"),sQuery(id+"F0.wireOp",EDGE,"E96.1.0.2"),sQuery(id+"F0.wireOp",EDGE,"E96.1.0.4"),sQuery(id+"F0.wireOp",EDGE,"E96.1.0.9"),sQuery(id+"F0.wireOp",EDGE,"E96.1.0.10"),sQuery(id+"F0.wireOp",EDGE,"E96.1.0.11"),sQuery(id+"F0.wireOp",EDGE,"E96.1.0.17"),sQuery(id+"F0.wireOp",EDGE,"E96.1.0.18"),sQuery(id+"F0.wireOp",EDGE,"E96.1.0.20"),sQuery(id+"F0.wireOp",EDGE,"E96.1.0.22"),sQuery(id+"F0.wireOp",EDGE,"E96.1.0.23"),sQuery(id+"F0.wireOp",EDGE,"E96.1.0.24"),sQuery(id+"F0.wireOp",EDGE,"E96.1.0.30"),sQuery(id+"F0.wireOp",EDGE,"E96.1.0.31"),sQuery(id+"F0.wireOp",EDGE,"E96.1.0.32"),sQuery(id+"F0.wireOp",EDGE,"E96.1.0.33"),sQuery(id+"F0.wireOp",EDGE,"E96.1.0.35"),sQuery(id+"F0.wireOp",EDGE,"E96.1.0.40"),sQuery(id+"F0.wireOp",EDGE,"E96.1.0.43"),sQuery(id+"F0.wireOp",EDGE,"E96.1.0.44"),sQuery(id+"F0.wireOp",EDGE,"E96.1.0.45"),sQuery(id+"F0.wireOp",EDGE,"E96.1.0.46"),sQuery(id+"F0.wireOp",EDGE,"E96.1.0.47"),sQuery(id+"F0.wireOp",EDGE,"E96.1.0.49"),sQuery(id+"F0.wireOp",EDGE,"E96.1.0.51"),sQuery(id+"F0.wireOp",EDGE,"E96.1.0.54"),sQuery(id+"F0.wireOp",EDGE,"E96.1.0.55"),sQuery(id+"F0.wireOp",EDGE,"E96.1.0.58"),sQuery(id+"F0.wireOp",EDGE,"E96.1.0.59"),sQuery(id+"F0.wireOp",EDGE,"E96.1.0.60"),sQuery(id+"F0.wireOp",EDGE,"E96.1.0.61"),sQuery(id+"F0.wireOp",EDGE,"E79.trimOffspring"),sQuery(id+"F0.wireOp",EDGE,"E96.1.0.66"),sQuery(id+"F0.wireOp",EDGE,"E96.1.0.67"),sQuery(id+"F0.wireOp",EDGE,"E96.1.0.68"),sQuery(id+"F0.wireOp",EDGE,"E96.1.0.69"),sQuery(id+"F0.wireOp",EDGE,"E96.1.0.70"),sQuery(id+"F0.wireOp",EDGE,"E96.1.0.71"),sQuery(id+"F0.wireOp",EDGE,"E96.1.0.72"),sQuery(id+"F0.wireOp",EDGE,"E96.1.0.73"),sQuery(id+"F0.wireOp",EDGE,"E96.1.0.74"),sQuery(id+"F0.wireOp",EDGE,"E96.1.0.75"),sQuery(id+"F0.wireOp",EDGE,"E96.1.0.76"),sQuery(id+"F0.wireOp",EDGE,"E96.1.0.77"),sQuery(id+"F0.wireOp",EDGE,"E96.1.0.78"),sQuery(id+"F0.wireOp",EDGE,"E96.1.0.79"),sQuery(id+"F0.wireOp",EDGE,"E96.1.0.80"),sQuery(id+"F0.wireOp",EDGE,"E96.1.0.81"),sQuery(id+"F0.wireOp",EDGE,"E96.1.0.82"),sQuery(id+"F0.wireOp",EDGE,"E96.1.0.83"),sQuery(id+"F0.wireOp",EDGE,"E96.1.0.84"),sQuery(id+"F0.wireOp",EDGE,"E96.1.0.85"),sQuery(id+"F0.wireOp",EDGE,"E96.1.0.86"),sQuery(id+"F0.wireOp",EDGE,"E96.1.0.87"),sQuery(id+"F0.wireOp",EDGE,"E96.1.0.88"),sQuery(id+"F0.wireOp",EDGE,"E96.1.0.89"),sQuery(id+"F0.wireOp",EDGE,"E96.1.0.90"),sQuery(id+"F0.wireOp",EDGE,"E96.1.0.91"),sQuery(id+"F0.wireOp",EDGE,"E60.left"),sQuery(id+"F0.wireOp",EDGE,"E80.trimOffspring")])]});
            var Q1;
            Q1=makeQuery(id+"F1.opExtrude","SWEPT_BODY",BODY,{"disambiguationData":[OSD([sQuery(id+"F0.wireOp",EDGE,"E96.2.1.0"),sQuery(id+"F0.wireOp",EDGE,"E96.2.1.2"),sQuery(id+"F0.wireOp",EDGE,"E96.2.1.4"),sQuery(id+"F0.wireOp",EDGE,"E96.2.1.9"),sQuery(id+"F0.wireOp",EDGE,"E96.2.1.10"),sQuery(id+"F0.wireOp",EDGE,"E96.2.1.11"),sQuery(id+"F0.wireOp",EDGE,"E96.2.1.17"),sQuery(id+"F0.wireOp",EDGE,"E96.2.1.18"),sQuery(id+"F0.wireOp",EDGE,"E96.2.1.20"),sQuery(id+"F0.wireOp",EDGE,"E96.2.1.22"),sQuery(id+"F0.wireOp",EDGE,"E96.2.1.23"),sQuery(id+"F0.wireOp",EDGE,"E96.2.1.24"),sQuery(id+"F0.wireOp",EDGE,"E96.2.1.30"),sQuery(id+"F0.wireOp",EDGE,"E96.2.1.31"),sQuery(id+"F0.wireOp",EDGE,"E96.2.1.32"),sQuery(id+"F0.wireOp",EDGE,"E96.2.1.33"),sQuery(id+"F0.wireOp",EDGE,"E96.2.1.35"),sQuery(id+"F0.wireOp",EDGE,"E96.2.1.40"),sQuery(id+"F0.wireOp",EDGE,"E96.2.1.43"),sQuery(id+"F0.wireOp",EDGE,"E96.2.1.44"),sQuery(id+"F0.wireOp",EDGE,"E96.2.1.45"),sQuery(id+"F0.wireOp",EDGE,"E96.2.1.46"),sQuery(id+"F0.wireOp",EDGE,"E96.2.1.47"),sQuery(id+"F0.wireOp",EDGE,"E96.2.1.49"),sQuery(id+"F0.wireOp",EDGE,"E96.2.1.51"),sQuery(id+"F0.wireOp",EDGE,"E96.2.1.54"),sQuery(id+"F0.wireOp",EDGE,"E96.2.1.55"),sQuery(id+"F0.wireOp",EDGE,"E96.2.1.58"),sQuery(id+"F0.wireOp",EDGE,"E96.2.1.59"),sQuery(id+"F0.wireOp",EDGE,"E96.2.1.60"),sQuery(id+"F0.wireOp",EDGE,"E96.2.1.61"),sQuery(id+"F0.wireOp",EDGE,"E96.2.1.65"),sQuery(id+"F0.wireOp",EDGE,"E96.2.1.66"),sQuery(id+"F0.wireOp",EDGE,"E96.2.1.67"),sQuery(id+"F0.wireOp",EDGE,"E96.2.1.68"),sQuery(id+"F0.wireOp",EDGE,"E96.2.1.69"),sQuery(id+"F0.wireOp",EDGE,"E96.2.1.70"),sQuery(id+"F0.wireOp",EDGE,"E96.2.1.71"),sQuery(id+"F0.wireOp",EDGE,"E96.2.1.72"),sQuery(id+"F0.wireOp",EDGE,"E96.2.1.73"),sQuery(id+"F0.wireOp",EDGE,"E96.2.1.74"),sQuery(id+"F0.wireOp",EDGE,"E96.2.1.75"),sQuery(id+"F0.wireOp",EDGE,"E96.2.1.76"),sQuery(id+"F0.wireOp",EDGE,"E96.2.1.77"),sQuery(id+"F0.wireOp",EDGE,"E96.2.1.78"),sQuery(id+"F0.wireOp",EDGE,"E96.2.1.79"),sQuery(id+"F0.wireOp",EDGE,"E96.2.1.80"),sQuery(id+"F0.wireOp",EDGE,"E96.2.1.81"),sQuery(id+"F0.wireOp",EDGE,"E96.2.1.82"),sQuery(id+"F0.wireOp",EDGE,"E96.2.1.83"),sQuery(id+"F0.wireOp",EDGE,"E96.2.1.84"),sQuery(id+"F0.wireOp",EDGE,"E96.2.1.85"),sQuery(id+"F0.wireOp",EDGE,"E96.2.1.86"),sQuery(id+"F0.wireOp",EDGE,"E96.2.1.87"),sQuery(id+"F0.wireOp",EDGE,"E96.2.1.88"),sQuery(id+"F0.wireOp",EDGE,"E96.2.1.89"),sQuery(id+"F0.wireOp",EDGE,"E96.2.1.90"),sQuery(id+"F0.wireOp",EDGE,"E96.2.1.91"),sQuery(id+"F0.wireOp",EDGE,"E96.2.1.94"),sQuery(id+"F0.wireOp",EDGE,"E96.2.1.95")])]});
            var Q2;
            Q2=makeQuery(id+"F1.opExtrude","SWEPT_BODY",BODY,{"disambiguationData":[OSD([sQuery(id+"F0.wireOp",EDGE,"E96.2.0.0"),sQuery(id+"F0.wireOp",EDGE,"E96.2.0.2"),sQuery(id+"F0.wireOp",EDGE,"E96.2.0.4"),sQuery(id+"F0.wireOp",EDGE,"E96.2.0.9"),sQuery(id+"F0.wireOp",EDGE,"E96.2.0.10"),sQuery(id+"F0.wireOp",EDGE,"E96.2.0.11"),sQuery(id+"F0.wireOp",EDGE,"E96.2.0.17"),sQuery(id+"F0.wireOp",EDGE,"E96.2.0.18"),sQuery(id+"F0.wireOp",EDGE,"E96.2.0.20"),sQuery(id+"F0.wireOp",EDGE,"E96.2.0.22"),sQuery(id+"F0.wireOp",EDGE,"E96.2.0.23"),sQuery(id+"F0.wireOp",EDGE,"E96.2.0.24"),sQuery(id+"F0.wireOp",EDGE,"E96.2.0.30"),sQuery(id+"F0.wireOp",EDGE,"E96.2.0.31"),sQuery(id+"F0.wireOp",EDGE,"E96.2.0.32"),sQuery(id+"F0.wireOp",EDGE,"E96.2.0.33"),sQuery(id+"F0.wireOp",EDGE,"E96.2.0.35"),sQuery(id+"F0.wireOp",EDGE,"E96.2.0.40"),sQuery(id+"F0.wireOp",EDGE,"E96.2.0.43"),sQuery(id+"F0.wireOp",EDGE,"E96.2.0.44"),sQuery(id+"F0.wireOp",EDGE,"E96.2.0.45"),sQuery(id+"F0.wireOp",EDGE,"E96.2.0.46"),sQuery(id+"F0.wireOp",EDGE,"E96.2.0.47"),sQuery(id+"F0.wireOp",EDGE,"E96.2.0.49"),sQuery(id+"F0.wireOp",EDGE,"E96.2.0.51"),sQuery(id+"F0.wireOp",EDGE,"E96.2.0.54"),sQuery(id+"F0.wireOp",EDGE,"E96.2.0.55"),sQuery(id+"F0.wireOp",EDGE,"E96.2.0.58"),sQuery(id+"F0.wireOp",EDGE,"E96.2.0.59"),sQuery(id+"F0.wireOp",EDGE,"E96.2.0.60"),sQuery(id+"F0.wireOp",EDGE,"E96.2.0.61"),sQuery(id+"F0.wireOp",EDGE,"E96.2.0.65"),sQuery(id+"F0.wireOp",EDGE,"E96.2.0.66"),sQuery(id+"F0.wireOp",EDGE,"E96.2.0.67"),sQuery(id+"F0.wireOp",EDGE,"E96.2.0.68"),sQuery(id+"F0.wireOp",EDGE,"E96.2.0.69"),sQuery(id+"F0.wireOp",EDGE,"E96.2.0.70"),sQuery(id+"F0.wireOp",EDGE,"E96.2.0.71"),sQuery(id+"F0.wireOp",EDGE,"E96.2.0.72"),sQuery(id+"F0.wireOp",EDGE,"E96.2.0.73"),sQuery(id+"F0.wireOp",EDGE,"E96.2.0.74"),sQuery(id+"F0.wireOp",EDGE,"E96.2.0.75"),sQuery(id+"F0.wireOp",EDGE,"E96.2.0.76"),sQuery(id+"F0.wireOp",EDGE,"E96.2.0.77"),sQuery(id+"F0.wireOp",EDGE,"E96.2.0.78"),sQuery(id+"F0.wireOp",EDGE,"E96.2.0.79"),sQuery(id+"F0.wireOp",EDGE,"E96.2.0.80"),sQuery(id+"F0.wireOp",EDGE,"E96.2.0.81"),sQuery(id+"F0.wireOp",EDGE,"E96.2.0.82"),sQuery(id+"F0.wireOp",EDGE,"E96.2.0.83"),sQuery(id+"F0.wireOp",EDGE,"E96.2.0.84"),sQuery(id+"F0.wireOp",EDGE,"E96.2.0.85"),sQuery(id+"F0.wireOp",EDGE,"E96.2.0.86"),sQuery(id+"F0.wireOp",EDGE,"E96.2.0.87"),sQuery(id+"F0.wireOp",EDGE,"E96.2.0.88"),sQuery(id+"F0.wireOp",EDGE,"E96.2.0.89"),sQuery(id+"F0.wireOp",EDGE,"E96.2.0.90"),sQuery(id+"F0.wireOp",EDGE,"E96.2.0.91"),sQuery(id+"F0.wireOp",EDGE,"E96.2.0.94"),sQuery(id+"F0.wireOp",EDGE,"E96.2.0.95")])]});
            var Q3;
            Q3=makeQuery(id+"F1.opExtrude","SWEPT_BODY",BODY,{"disambiguationData":[OSD([sQuery(id+"F0.wireOp",EDGE,"E0.bottom"),sQuery(id+"F0.wireOp",EDGE,"E0.top"),sQuery(id+"F0.wireOp",EDGE,"E0.left"),sQuery(id+"F0.wireOp",EDGE,"E0.right"),sQuery(id+"F0.wireOp",EDGE,"E1.filletArc"),sQuery(id+"F0.wireOp",EDGE,"E2.filletArc"),sQuery(id+"F0.wireOp",EDGE,"E3.filletArc"),sQuery(id+"F0.wireOp",EDGE,"E4.filletArc"),sQuery(id+"F0.wireOp",EDGE,"E5.MirrorCS"),sQuery(id+"F0.wireOp",EDGE,"E6.MirrorCS"),sQuery(id+"F0.wireOp",EDGE,"E7.MirrorCS"),sQuery(id+"F0.wireOp",EDGE,"E8.MirrorCS"),sQuery(id+"F0.wireOp",EDGE,"E9.MirrorCS"),sQuery(id+"F0.wireOp",EDGE,"E10.MirrorCS"),sQuery(id+"F0.wireOp",EDGE,"E15.MirrorCS"),sQuery(id+"F0.wireOp",EDGE,"E16.MirrorCS"),sQuery(id+"F0.wireOp",EDGE,"E17.MirrorCS"),sQuery(id+"F0.wireOp",EDGE,"E18.MirrorCS"),sQuery(id+"F0.wireOp",EDGE,"E19.MirrorCS"),sQuery(id+"F0.wireOp",EDGE,"E20.MirrorCS"),sQuery(id+"F0.wireOp",EDGE,"E21.MirrorCS"),sQuery(id+"F0.wireOp",EDGE,"E22.MirrorCS"),sQuery(id+"F0.wireOp",EDGE,"E23.MirrorCS"),sQuery(id+"F0.wireOp",EDGE,"E24.MirrorCS"),sQuery(id+"F0.wireOp",EDGE,"E26.MirrorCS"),sQuery(id+"F0.wireOp",EDGE,"E27.MirrorCS"),sQuery(id+"F0.wireOp",EDGE,"E29.MirrorCS"),sQuery(id+"F0.wireOp",EDGE,"E30.MirrorCS"),sQuery(id+"F0.wireOp",EDGE,"E31.MirrorCS"),sQuery(id+"F0.wireOp",EDGE,"E33.MirrorCS"),sQuery(id+"F0.wireOp",EDGE,"E34.MirrorCS"),sQuery(id+"F0.wireOp",EDGE,"E40.MirrorCS"),sQuery(id+"F0.wireOp",EDGE,"E42.MirrorCS"),sQuery(id+"F0.wireOp",EDGE,"E43.MirrorCS"),sQuery(id+"F0.wireOp",EDGE,"E44.MirrorCS"),sQuery(id+"F0.wireOp",EDGE,"E45.MirrorCS"),sQuery(id+"F0.wireOp",EDGE,"E46.MirrorCS"),sQuery(id+"F0.wireOp",EDGE,"E47.MirrorCS"),sQuery(id+"F0.wireOp",EDGE,"E52.MirrorCS"),sQuery(id+"F0.wireOp",EDGE,"E55.MirrorCS"),sQuery(id+"F0.wireOp",EDGE,"E56.MirrorCS"),sQuery(id+"F0.wireOp",EDGE,"E58.MirrorCS"),sQuery(id+"F0.wireOp",EDGE,"E60.bottom"),sQuery(id+"F0.wireOp",EDGE,"E60.top"),sQuery(id+"F0.wireOp",EDGE,"E60.left"),sQuery(id+"F0.wireOp",EDGE,"E61.MirrorCS"),sQuery(id+"F0.wireOp",EDGE,"E62.MirrorCS"),sQuery(id+"F0.wireOp",EDGE,"E63.MirrorCS"),sQuery(id+"F0.wireOp",EDGE,"E64.MirrorCS"),sQuery(id+"F0.wireOp",EDGE,"E66.MirrorCS"),sQuery(id+"F0.wireOp",EDGE,"E68.MirrorCS"),sQuery(id+"F0.wireOp",EDGE,"E60.right"),sQuery(id+"F0.wireOp",EDGE,"E73.MirrorCS"),sQuery(id+"F0.wireOp",EDGE,"E76.MirrorCS"),sQuery(id+"F0.wireOp",EDGE,"E77.MirrorCS"),sQuery(id+"F0.wireOp",EDGE,"E78.MirrorCS"),sQuery(id+"F0.wireOp",EDGE,"E79.trimOffspring"),sQuery(id+"F0.wireOp",EDGE,"E80.trimOffspring"),sQuery(id+"F0.wireOp",EDGE,"E89.trimOffspring"),sQuery(id+"F0.wireOp",EDGE,"E95.trimOffspring")])]});
            var Q4;
            Q4=makeQuery(id+"F1.opExtrude","SWEPT_BODY",BODY,{"disambiguationData":[OSD([sQuery(id+"F0.wireOp",EDGE,"E96.2.2.0"),sQuery(id+"F0.wireOp",EDGE,"E96.2.2.2"),sQuery(id+"F0.wireOp",EDGE,"E96.2.2.4"),sQuery(id+"F0.wireOp",EDGE,"E96.2.2.9"),sQuery(id+"F0.wireOp",EDGE,"E96.2.2.10"),sQuery(id+"F0.wireOp",EDGE,"E96.2.2.11"),sQuery(id+"F0.wireOp",EDGE,"E96.2.2.17"),sQuery(id+"F0.wireOp",EDGE,"E96.2.2.18"),sQuery(id+"F0.wireOp",EDGE,"E96.2.2.20"),sQuery(id+"F0.wireOp",EDGE,"E96.2.2.22"),sQuery(id+"F0.wireOp",EDGE,"E96.2.2.23"),sQuery(id+"F0.wireOp",EDGE,"E96.2.2.24"),sQuery(id+"F0.wireOp",EDGE,"E96.2.2.30"),sQuery(id+"F0.wireOp",EDGE,"E96.2.2.31"),sQuery(id+"F0.wireOp",EDGE,"E96.2.2.32"),sQuery(id+"F0.wireOp",EDGE,"E96.2.2.33"),sQuery(id+"F0.wireOp",EDGE,"E96.2.2.35"),sQuery(id+"F0.wireOp",EDGE,"E96.2.2.40"),sQuery(id+"F0.wireOp",EDGE,"E96.2.2.43"),sQuery(id+"F0.wireOp",EDGE,"E96.2.2.44"),sQuery(id+"F0.wireOp",EDGE,"E96.2.2.45"),sQuery(id+"F0.wireOp",EDGE,"E96.2.2.46"),sQuery(id+"F0.wireOp",EDGE,"E96.2.2.47"),sQuery(id+"F0.wireOp",EDGE,"E96.2.2.49"),sQuery(id+"F0.wireOp",EDGE,"E96.2.2.51"),sQuery(id+"F0.wireOp",EDGE,"E96.2.2.54"),sQuery(id+"F0.wireOp",EDGE,"E96.2.2.55"),sQuery(id+"F0.wireOp",EDGE,"E96.2.2.58"),sQuery(id+"F0.wireOp",EDGE,"E96.2.2.59"),sQuery(id+"F0.wireOp",EDGE,"E96.2.2.60"),sQuery(id+"F0.wireOp",EDGE,"E96.2.2.61"),sQuery(id+"F0.wireOp",EDGE,"E96.2.2.65"),sQuery(id+"F0.wireOp",EDGE,"E96.2.2.66"),sQuery(id+"F0.wireOp",EDGE,"E96.2.2.67"),sQuery(id+"F0.wireOp",EDGE,"E96.2.2.68"),sQuery(id+"F0.wireOp",EDGE,"E96.2.2.69"),sQuery(id+"F0.wireOp",EDGE,"E96.2.2.70"),sQuery(id+"F0.wireOp",EDGE,"E96.2.2.71"),sQuery(id+"F0.wireOp",EDGE,"E96.2.2.72"),sQuery(id+"F0.wireOp",EDGE,"E96.2.2.73"),sQuery(id+"F0.wireOp",EDGE,"E96.2.2.74"),sQuery(id+"F0.wireOp",EDGE,"E96.2.2.75"),sQuery(id+"F0.wireOp",EDGE,"E96.2.2.76"),sQuery(id+"F0.wireOp",EDGE,"E96.2.2.77"),sQuery(id+"F0.wireOp",EDGE,"E96.2.2.78"),sQuery(id+"F0.wireOp",EDGE,"E96.2.2.79"),sQuery(id+"F0.wireOp",EDGE,"E96.2.2.80"),sQuery(id+"F0.wireOp",EDGE,"E96.2.2.81"),sQuery(id+"F0.wireOp",EDGE,"E96.2.2.82"),sQuery(id+"F0.wireOp",EDGE,"E96.2.2.83"),sQuery(id+"F0.wireOp",EDGE,"E96.2.2.84"),sQuery(id+"F0.wireOp",EDGE,"E96.2.2.85"),sQuery(id+"F0.wireOp",EDGE,"E96.2.2.86"),sQuery(id+"F0.wireOp",EDGE,"E96.2.2.87"),sQuery(id+"F0.wireOp",EDGE,"E96.2.2.88"),sQuery(id+"F0.wireOp",EDGE,"E96.2.2.89"),sQuery(id+"F0.wireOp",EDGE,"E96.2.2.90"),sQuery(id+"F0.wireOp",EDGE,"E96.2.2.91"),sQuery(id+"F0.wireOp",EDGE,"E96.2.2.94"),sQuery(id+"F0.wireOp",EDGE,"E96.2.2.95")])]});
            var Q5;
            Q5=makeQuery(id+"F1.opExtrude","SWEPT_BODY",BODY,{"disambiguationData":[OSD([sQuery(id+"F0.wireOp",EDGE,"E96.1.1.0"),sQuery(id+"F0.wireOp",EDGE,"E96.1.1.2"),sQuery(id+"F0.wireOp",EDGE,"E96.1.1.4"),sQuery(id+"F0.wireOp",EDGE,"E96.1.1.9"),sQuery(id+"F0.wireOp",EDGE,"E96.1.1.10"),sQuery(id+"F0.wireOp",EDGE,"E96.1.1.11"),sQuery(id+"F0.wireOp",EDGE,"E96.1.1.17"),sQuery(id+"F0.wireOp",EDGE,"E96.1.1.18"),sQuery(id+"F0.wireOp",EDGE,"E96.1.1.20"),sQuery(id+"F0.wireOp",EDGE,"E96.1.1.22"),sQuery(id+"F0.wireOp",EDGE,"E96.1.1.23"),sQuery(id+"F0.wireOp",EDGE,"E96.1.1.24"),sQuery(id+"F0.wireOp",EDGE,"E96.1.1.30"),sQuery(id+"F0.wireOp",EDGE,"E96.1.1.31"),sQuery(id+"F0.wireOp",EDGE,"E96.1.1.32"),sQuery(id+"F0.wireOp",EDGE,"E96.1.1.33"),sQuery(id+"F0.wireOp",EDGE,"E96.1.1.35"),sQuery(id+"F0.wireOp",EDGE,"E96.1.1.40"),sQuery(id+"F0.wireOp",EDGE,"E96.1.1.43"),sQuery(id+"F0.wireOp",EDGE,"E96.1.1.44"),sQuery(id+"F0.wireOp",EDGE,"E96.1.1.45"),sQuery(id+"F0.wireOp",EDGE,"E96.1.1.46"),sQuery(id+"F0.wireOp",EDGE,"E96.1.1.47"),sQuery(id+"F0.wireOp",EDGE,"E96.1.1.49"),sQuery(id+"F0.wireOp",EDGE,"E96.1.1.51"),sQuery(id+"F0.wireOp",EDGE,"E96.1.1.54"),sQuery(id+"F0.wireOp",EDGE,"E96.1.1.55"),sQuery(id+"F0.wireOp",EDGE,"E96.1.1.58"),sQuery(id+"F0.wireOp",EDGE,"E96.1.1.59"),sQuery(id+"F0.wireOp",EDGE,"E96.1.1.60"),sQuery(id+"F0.wireOp",EDGE,"E96.1.1.61"),sQuery(id+"F0.wireOp",EDGE,"E96.1.1.65"),sQuery(id+"F0.wireOp",EDGE,"E96.1.1.66"),sQuery(id+"F0.wireOp",EDGE,"E96.1.1.67"),sQuery(id+"F0.wireOp",EDGE,"E96.1.1.68"),sQuery(id+"F0.wireOp",EDGE,"E96.1.1.69"),sQuery(id+"F0.wireOp",EDGE,"E96.1.1.70"),sQuery(id+"F0.wireOp",EDGE,"E96.1.1.71"),sQuery(id+"F0.wireOp",EDGE,"E96.1.1.72"),sQuery(id+"F0.wireOp",EDGE,"E96.1.1.73"),sQuery(id+"F0.wireOp",EDGE,"E96.1.1.74"),sQuery(id+"F0.wireOp",EDGE,"E96.1.1.75"),sQuery(id+"F0.wireOp",EDGE,"E96.1.1.76"),sQuery(id+"F0.wireOp",EDGE,"E96.1.1.77"),sQuery(id+"F0.wireOp",EDGE,"E96.1.1.78"),sQuery(id+"F0.wireOp",EDGE,"E96.1.1.79"),sQuery(id+"F0.wireOp",EDGE,"E96.1.1.80"),sQuery(id+"F0.wireOp",EDGE,"E96.1.1.81"),sQuery(id+"F0.wireOp",EDGE,"E96.1.1.82"),sQuery(id+"F0.wireOp",EDGE,"E96.1.1.83"),sQuery(id+"F0.wireOp",EDGE,"E96.1.1.84"),sQuery(id+"F0.wireOp",EDGE,"E96.1.1.85"),sQuery(id+"F0.wireOp",EDGE,"E96.1.1.86"),sQuery(id+"F0.wireOp",EDGE,"E96.1.1.87"),sQuery(id+"F0.wireOp",EDGE,"E96.1.1.88"),sQuery(id+"F0.wireOp",EDGE,"E96.1.1.89"),sQuery(id+"F0.wireOp",EDGE,"E96.1.1.90"),sQuery(id+"F0.wireOp",EDGE,"E96.1.1.91"),sQuery(id+"F0.wireOp",EDGE,"E96.1.1.94"),sQuery(id+"F0.wireOp",EDGE,"E96.1.1.95")])]});
            var Q6;
            Q6=makeQuery(id+"F1.opExtrude","SWEPT_BODY",BODY,{"disambiguationData":[OSD([sQuery(id+"F0.wireOp",EDGE,"E96.1.2.0"),sQuery(id+"F0.wireOp",EDGE,"E96.1.2.2"),sQuery(id+"F0.wireOp",EDGE,"E96.1.2.4"),sQuery(id+"F0.wireOp",EDGE,"E96.1.2.9"),sQuery(id+"F0.wireOp",EDGE,"E96.1.2.10"),sQuery(id+"F0.wireOp",EDGE,"E96.1.2.11"),sQuery(id+"F0.wireOp",EDGE,"E96.1.2.17"),sQuery(id+"F0.wireOp",EDGE,"E96.1.2.18"),sQuery(id+"F0.wireOp",EDGE,"E96.1.2.20"),sQuery(id+"F0.wireOp",EDGE,"E96.1.2.22"),sQuery(id+"F0.wireOp",EDGE,"E96.1.2.23"),sQuery(id+"F0.wireOp",EDGE,"E96.1.2.24"),sQuery(id+"F0.wireOp",EDGE,"E96.1.2.30"),sQuery(id+"F0.wireOp",EDGE,"E96.1.2.31"),sQuery(id+"F0.wireOp",EDGE,"E96.1.2.32"),sQuery(id+"F0.wireOp",EDGE,"E96.1.2.33"),sQuery(id+"F0.wireOp",EDGE,"E96.1.2.35"),sQuery(id+"F0.wireOp",EDGE,"E96.1.2.40"),sQuery(id+"F0.wireOp",EDGE,"E96.1.2.43"),sQuery(id+"F0.wireOp",EDGE,"E96.1.2.44"),sQuery(id+"F0.wireOp",EDGE,"E96.1.2.45"),sQuery(id+"F0.wireOp",EDGE,"E96.1.2.46"),sQuery(id+"F0.wireOp",EDGE,"E96.1.2.47"),sQuery(id+"F0.wireOp",EDGE,"E96.1.2.49"),sQuery(id+"F0.wireOp",EDGE,"E96.1.2.51"),sQuery(id+"F0.wireOp",EDGE,"E96.1.2.54"),sQuery(id+"F0.wireOp",EDGE,"E96.1.2.55"),sQuery(id+"F0.wireOp",EDGE,"E96.1.2.58"),sQuery(id+"F0.wireOp",EDGE,"E96.1.2.59"),sQuery(id+"F0.wireOp",EDGE,"E96.1.2.60"),sQuery(id+"F0.wireOp",EDGE,"E96.1.2.61"),sQuery(id+"F0.wireOp",EDGE,"E96.1.2.65"),sQuery(id+"F0.wireOp",EDGE,"E96.1.2.66"),sQuery(id+"F0.wireOp",EDGE,"E96.1.2.67"),sQuery(id+"F0.wireOp",EDGE,"E96.1.2.68"),sQuery(id+"F0.wireOp",EDGE,"E96.1.2.69"),sQuery(id+"F0.wireOp",EDGE,"E96.1.2.70"),sQuery(id+"F0.wireOp",EDGE,"E96.1.2.71"),sQuery(id+"F0.wireOp",EDGE,"E96.1.2.72"),sQuery(id+"F0.wireOp",EDGE,"E96.1.2.73"),sQuery(id+"F0.wireOp",EDGE,"E96.1.2.74"),sQuery(id+"F0.wireOp",EDGE,"E96.1.2.75"),sQuery(id+"F0.wireOp",EDGE,"E96.1.2.76"),sQuery(id+"F0.wireOp",EDGE,"E96.1.2.77"),sQuery(id+"F0.wireOp",EDGE,"E96.1.2.78"),sQuery(id+"F0.wireOp",EDGE,"E96.1.2.79"),sQuery(id+"F0.wireOp",EDGE,"E96.1.2.80"),sQuery(id+"F0.wireOp",EDGE,"E96.1.2.81"),sQuery(id+"F0.wireOp",EDGE,"E96.1.2.82"),sQuery(id+"F0.wireOp",EDGE,"E96.1.2.83"),sQuery(id+"F0.wireOp",EDGE,"E96.1.2.84"),sQuery(id+"F0.wireOp",EDGE,"E96.1.2.85"),sQuery(id+"F0.wireOp",EDGE,"E96.1.2.86"),sQuery(id+"F0.wireOp",EDGE,"E96.1.2.87"),sQuery(id+"F0.wireOp",EDGE,"E96.1.2.88"),sQuery(id+"F0.wireOp",EDGE,"E96.1.2.89"),sQuery(id+"F0.wireOp",EDGE,"E96.1.2.90"),sQuery(id+"F0.wireOp",EDGE,"E96.1.2.91"),sQuery(id+"F0.wireOp",EDGE,"E96.1.2.94"),sQuery(id+"F0.wireOp",EDGE,"E96.1.2.95")])]});
            var Q7;
            Q7=makeQuery(id+"F1.opExtrude","SWEPT_BODY",BODY,{"disambiguationData":[OSD([sQuery(id+"F0.wireOp",EDGE,"E96.0.1.0"),sQuery(id+"F0.wireOp",EDGE,"E96.0.1.2"),sQuery(id+"F0.wireOp",EDGE,"E96.0.1.4"),sQuery(id+"F0.wireOp",EDGE,"E96.0.1.9"),sQuery(id+"F0.wireOp",EDGE,"E96.0.1.10"),sQuery(id+"F0.wireOp",EDGE,"E96.0.1.11"),sQuery(id+"F0.wireOp",EDGE,"E96.0.1.17"),sQuery(id+"F0.wireOp",EDGE,"E96.0.1.18"),sQuery(id+"F0.wireOp",EDGE,"E96.0.1.20"),sQuery(id+"F0.wireOp",EDGE,"E96.0.1.22"),sQuery(id+"F0.wireOp",EDGE,"E96.0.1.23"),sQuery(id+"F0.wireOp",EDGE,"E96.0.1.24"),sQuery(id+"F0.wireOp",EDGE,"E96.0.1.30"),sQuery(id+"F0.wireOp",EDGE,"E96.0.1.31"),sQuery(id+"F0.wireOp",EDGE,"E96.0.1.32"),sQuery(id+"F0.wireOp",EDGE,"E96.0.1.33"),sQuery(id+"F0.wireOp",EDGE,"E96.0.1.35"),sQuery(id+"F0.wireOp",EDGE,"E96.0.1.40"),sQuery(id+"F0.wireOp",EDGE,"E96.0.1.43"),sQuery(id+"F0.wireOp",EDGE,"E96.0.1.44"),sQuery(id+"F0.wireOp",EDGE,"E96.0.1.45"),sQuery(id+"F0.wireOp",EDGE,"E96.0.1.46"),sQuery(id+"F0.wireOp",EDGE,"E96.0.1.47"),sQuery(id+"F0.wireOp",EDGE,"E96.0.1.49"),sQuery(id+"F0.wireOp",EDGE,"E96.0.1.51"),sQuery(id+"F0.wireOp",EDGE,"E96.0.1.54"),sQuery(id+"F0.wireOp",EDGE,"E96.0.1.55"),sQuery(id+"F0.wireOp",EDGE,"E96.0.1.58"),sQuery(id+"F0.wireOp",EDGE,"E96.0.1.59"),sQuery(id+"F0.wireOp",EDGE,"E96.0.1.60"),sQuery(id+"F0.wireOp",EDGE,"E96.0.1.61"),sQuery(id+"F0.wireOp",EDGE,"E96.0.1.65"),sQuery(id+"F0.wireOp",EDGE,"E96.0.1.66"),sQuery(id+"F0.wireOp",EDGE,"E96.0.1.67"),sQuery(id+"F0.wireOp",EDGE,"E96.0.1.68"),sQuery(id+"F0.wireOp",EDGE,"E96.0.1.69"),sQuery(id+"F0.wireOp",EDGE,"E96.0.1.70"),sQuery(id+"F0.wireOp",EDGE,"E96.0.1.71"),sQuery(id+"F0.wireOp",EDGE,"E96.0.1.72"),sQuery(id+"F0.wireOp",EDGE,"E96.0.1.73"),sQuery(id+"F0.wireOp",EDGE,"E96.0.1.74"),sQuery(id+"F0.wireOp",EDGE,"E96.0.1.75"),sQuery(id+"F0.wireOp",EDGE,"E96.0.1.76"),sQuery(id+"F0.wireOp",EDGE,"E96.0.1.77"),sQuery(id+"F0.wireOp",EDGE,"E96.0.1.78"),sQuery(id+"F0.wireOp",EDGE,"E96.0.1.79"),sQuery(id+"F0.wireOp",EDGE,"E96.0.1.80"),sQuery(id+"F0.wireOp",EDGE,"E96.0.1.81"),sQuery(id+"F0.wireOp",EDGE,"E96.0.1.82"),sQuery(id+"F0.wireOp",EDGE,"E96.0.1.83"),sQuery(id+"F0.wireOp",EDGE,"E96.0.1.84"),sQuery(id+"F0.wireOp",EDGE,"E96.0.1.85"),sQuery(id+"F0.wireOp",EDGE,"E96.0.1.86"),sQuery(id+"F0.wireOp",EDGE,"E96.0.1.87"),sQuery(id+"F0.wireOp",EDGE,"E96.0.1.88"),sQuery(id+"F0.wireOp",EDGE,"E96.0.1.89"),sQuery(id+"F0.wireOp",EDGE,"E96.0.1.90"),sQuery(id+"F0.wireOp",EDGE,"E96.0.1.91"),sQuery(id+"F0.wireOp",EDGE,"E96.0.1.94"),sQuery(id+"F0.wireOp",EDGE,"E96.0.1.95")])]});
            var Q8;
            Q8=makeQuery(id+"F1.opExtrude","SWEPT_BODY",BODY,{"disambiguationData":[OSD([sQuery(id+"F0.wireOp",EDGE,"E96.0.2.0"),sQuery(id+"F0.wireOp",EDGE,"E96.0.2.2"),sQuery(id+"F0.wireOp",EDGE,"E96.0.2.4"),sQuery(id+"F0.wireOp",EDGE,"E96.0.2.9"),sQuery(id+"F0.wireOp",EDGE,"E96.0.2.10"),sQuery(id+"F0.wireOp",EDGE,"E96.0.2.11"),sQuery(id+"F0.wireOp",EDGE,"E96.0.2.17"),sQuery(id+"F0.wireOp",EDGE,"E96.0.2.18"),sQuery(id+"F0.wireOp",EDGE,"E96.0.2.20"),sQuery(id+"F0.wireOp",EDGE,"E96.0.2.22"),sQuery(id+"F0.wireOp",EDGE,"E96.0.2.23"),sQuery(id+"F0.wireOp",EDGE,"E96.0.2.24"),sQuery(id+"F0.wireOp",EDGE,"E96.0.2.30"),sQuery(id+"F0.wireOp",EDGE,"E96.0.2.31"),sQuery(id+"F0.wireOp",EDGE,"E96.0.2.32"),sQuery(id+"F0.wireOp",EDGE,"E96.0.2.33"),sQuery(id+"F0.wireOp",EDGE,"E96.0.2.35"),sQuery(id+"F0.wireOp",EDGE,"E96.0.2.40"),sQuery(id+"F0.wireOp",EDGE,"E96.0.2.43"),sQuery(id+"F0.wireOp",EDGE,"E96.0.2.44"),sQuery(id+"F0.wireOp",EDGE,"E96.0.2.45"),sQuery(id+"F0.wireOp",EDGE,"E96.0.2.46"),sQuery(id+"F0.wireOp",EDGE,"E96.0.2.47"),sQuery(id+"F0.wireOp",EDGE,"E96.0.2.49"),sQuery(id+"F0.wireOp",EDGE,"E96.0.2.51"),sQuery(id+"F0.wireOp",EDGE,"E96.0.2.54"),sQuery(id+"F0.wireOp",EDGE,"E96.0.2.55"),sQuery(id+"F0.wireOp",EDGE,"E96.0.2.58"),sQuery(id+"F0.wireOp",EDGE,"E96.0.2.59"),sQuery(id+"F0.wireOp",EDGE,"E96.0.2.60"),sQuery(id+"F0.wireOp",EDGE,"E96.0.2.61"),sQuery(id+"F0.wireOp",EDGE,"E96.0.2.65"),sQuery(id+"F0.wireOp",EDGE,"E96.0.2.66"),sQuery(id+"F0.wireOp",EDGE,"E96.0.2.67"),sQuery(id+"F0.wireOp",EDGE,"E96.0.2.68"),sQuery(id+"F0.wireOp",EDGE,"E96.0.2.69"),sQuery(id+"F0.wireOp",EDGE,"E96.0.2.70"),sQuery(id+"F0.wireOp",EDGE,"E96.0.2.71"),sQuery(id+"F0.wireOp",EDGE,"E96.0.2.72"),sQuery(id+"F0.wireOp",EDGE,"E96.0.2.73"),sQuery(id+"F0.wireOp",EDGE,"E96.0.2.74"),sQuery(id+"F0.wireOp",EDGE,"E96.0.2.75"),sQuery(id+"F0.wireOp",EDGE,"E96.0.2.76"),sQuery(id+"F0.wireOp",EDGE,"E96.0.2.77"),sQuery(id+"F0.wireOp",EDGE,"E96.0.2.78"),sQuery(id+"F0.wireOp",EDGE,"E96.0.2.79"),sQuery(id+"F0.wireOp",EDGE,"E96.0.2.80"),sQuery(id+"F0.wireOp",EDGE,"E96.0.2.81"),sQuery(id+"F0.wireOp",EDGE,"E96.0.2.82"),sQuery(id+"F0.wireOp",EDGE,"E96.0.2.83"),sQuery(id+"F0.wireOp",EDGE,"E96.0.2.84"),sQuery(id+"F0.wireOp",EDGE,"E96.0.2.85"),sQuery(id+"F0.wireOp",EDGE,"E96.0.2.86"),sQuery(id+"F0.wireOp",EDGE,"E96.0.2.87"),sQuery(id+"F0.wireOp",EDGE,"E96.0.2.88"),sQuery(id+"F0.wireOp",EDGE,"E96.0.2.89"),sQuery(id+"F0.wireOp",EDGE,"E96.0.2.90"),sQuery(id+"F0.wireOp",EDGE,"E96.0.2.91"),sQuery(id+"F0.wireOp",EDGE,"E96.0.2.94"),sQuery(id+"F0.wireOp",EDGE,"E96.0.2.95")])]});
            var Q9;
            Q9=makeQuery(id+"F3.opExtrude","SWEPT_BODY",BODY,{"disambiguationData":[OSD([sQuery(id+"F2.wireOp",EDGE,"E97.bottom"),sQuery(id+"F2.wireOp",EDGE,"E97.top"),sQuery(id+"F2.wireOp",EDGE,"E97.left"),sQuery(id+"F2.wireOp",EDGE,"E97.right")])]});
            booleanBodies(context, id + "F5", {"operationType" : BooleanOperationType.SUBTRACTION, "tools" : qUnion([Q0, Q1, Q2, Q3, Q4, Q5, Q6, Q7, Q8]), "targets" : qUnion([Q9])});
        }
    });
